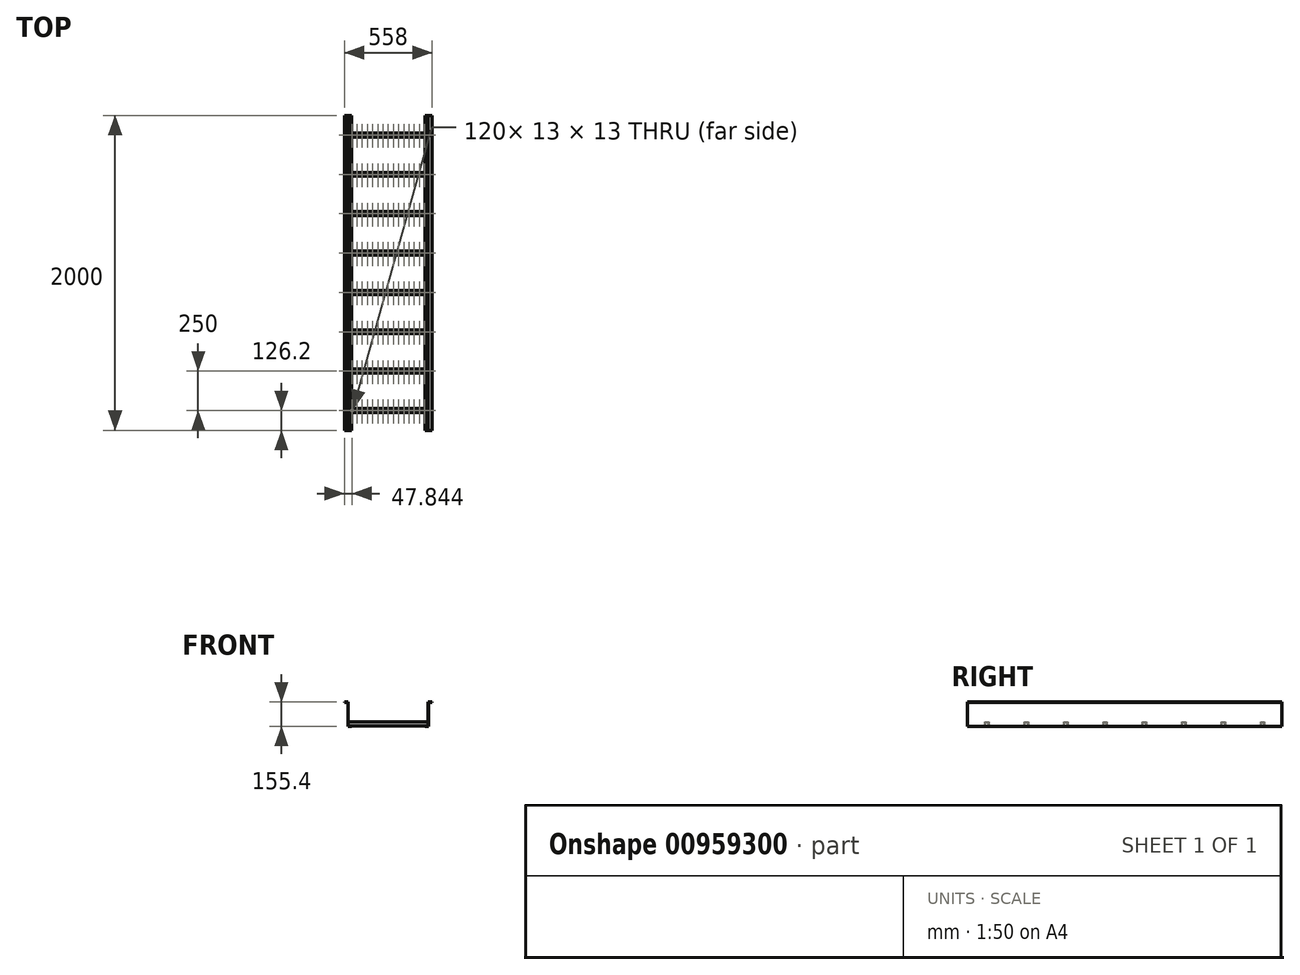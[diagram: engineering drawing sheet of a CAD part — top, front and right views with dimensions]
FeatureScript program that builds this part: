
annotation { "Feature Type Name" : "Feature", "Feature Type Description" : "" }
export const myFeature = defineFeature(function(context is Context, id is Id, definition is map)
    precondition{}
    {
        {
            var Q0;
            Q0=qCreatedBy(makeId("Front.planeOp"),FACE);
            var sketch = newSketch(context, id + "F0", { "sketchPlane" : qUnion([Q0])});
            skLineSegment(sketch, "E0", {"start": v(-136.9, 60.66) * mm, "end": v(-136.9, -91.74) * mm});
            skLineSegment(sketch, "E1", {"start": v(-136.9, -91.74) * mm, "end": v(-111.9, -91.74) * mm});
            skLineSegment(sketch, "E2", {"start": v(-111.9, -91.74) * mm, "end": v(-111.9, -88.74) * mm});
            skLineSegment(sketch, "E3", {"start": v(-111.9, -88.74) * mm, "end": v(-133.9, -88.74) * mm});
            skLineSegment(sketch, "E4", {"start": v(-133.9, -88.74) * mm, "end": v(-133.9, 63.66) * mm});
            skLineSegment(sketch, "E5", {"start": v(-133.9, 63.66) * mm, "end": v(-158.9, 63.66) * mm});
            skLineSegment(sketch, "E6", {"start": v(-158.9, 63.66) * mm, "end": v(-158.9, 60.66) * mm});
            skLineSegment(sketch, "E7", {"start": v(-158.9, 60.66) * mm, "end": v(-136.9, 60.66) * mm});
            skLineSegment(sketch, "E8", {"start": v(374.1, -88.74) * mm, "end": v(374.1, 63.66) * mm});
            skLineSegment(sketch, "E9", {"start": v(374.1, 63.66) * mm, "end": v(399.1, 63.66) * mm});
            skLineSegment(sketch, "E10", {"start": v(399.1, 63.66) * mm, "end": v(399.1, 60.66) * mm});
            skLineSegment(sketch, "E11", {"start": v(399.1, 60.66) * mm, "end": v(377.1, 60.66) * mm});
            skLineSegment(sketch, "E12", {"start": v(377.1, 60.66) * mm, "end": v(377.1, -91.74) * mm});
            skLineSegment(sketch, "E13", {"start": v(377.1, -91.74) * mm, "end": v(352.1, -91.74) * mm});
            skLineSegment(sketch, "E14", {"start": v(352.1, -91.74) * mm, "end": v(352.1, -88.74) * mm});
            skLineSegment(sketch, "E15", {"start": v(352.1, -88.74) * mm, "end": v(374.1, -88.74) * mm});
            skSolve(sketch);
        }
        {
            var Q0;
            Q0=makeQuery(id+"F0.imprint","IMPRINT",FACE,{"disambiguationData":[TD([[makeQuery(id+"F0.imprint","IMPRINT",EDGE,{"derivedFrom":sQuery(id+"F0.wireOp",EDGE,"E8")}),-1.0]])]});
            var Q1;
            Q1=makeQuery(id+"F0.imprint","IMPRINT",FACE,{"disambiguationData":[TD([[makeQuery(id+"F0.imprint","IMPRINT",EDGE,{"derivedFrom":sQuery(id+"F0.wireOp",EDGE,"E0")}),1.0]])]});
            extrude(context, id + "F1", {"entities" : qUnion([Q0, Q1]), "oppositeDirection" : true, "depth" : 2000 * mm, "offsetDistance" : 25 * mm});
        }
        {
            var Q0;
            Q0=makeQuery(id+"F1.opExtrude","SWEPT_FACE",FACE,{"disambiguationData":[OSD([sQuery(id+"F0.wireOp",EDGE,"E4")])]});
            var sketch = newSketch(context, id + "F2", { "sketchPlane" : qUnion([Q0])});
            skLineSegment(sketch, "E16", {"start": v(114, -88.74) * mm, "end": v(114, -64.34) * mm});
            skLineSegment(sketch, "E17", {"start": v(114, -64.34) * mm, "end": v(138.4, -64.34) * mm});
            skLineSegment(sketch, "E18", {"start": v(138.4, -64.34) * mm, "end": v(138.4, -88.74) * mm});
            skLineSegment(sketch, "E19", {"start": v(138.4, -88.74) * mm, "end": v(135.4, -88.74) * mm});
            skLineSegment(sketch, "E20", {"start": v(135.4, -88.74) * mm, "end": v(135.4, -67.34) * mm});
            skLineSegment(sketch, "E21", {"start": v(117, -88.74) * mm, "end": v(114, -88.74) * mm});
            skLineSegment(sketch, "E22", {"start": v(117, -88.74) * mm, "end": v(117, -67.34) * mm});
            skLineSegment(sketch, "E23", {"start": v(117, -67.34) * mm, "end": v(135.4, -67.34) * mm});
            skLineSegment(sketch, "E24.1.0.0", {"start": v(367, -67.34) * mm, "end": v(385.4, -67.34) * mm});
            skLineSegment(sketch, "E24.1.0.1", {"start": v(364, -64.34) * mm, "end": v(388.4, -64.34) * mm});
            skLineSegment(sketch, "E24.1.0.2", {"start": v(385.4, -88.74) * mm, "end": v(385.4, -67.34) * mm});
            skLineSegment(sketch, "E24.1.0.3", {"start": v(388.4, -64.34) * mm, "end": v(388.4, -88.74) * mm});
            skLineSegment(sketch, "E24.1.0.4", {"start": v(367, -88.74) * mm, "end": v(367, -67.34) * mm});
            skLineSegment(sketch, "E24.1.0.5", {"start": v(364, -88.74) * mm, "end": v(364, -64.34) * mm});
            skLineSegment(sketch, "E24.1.0.6", {"start": v(367, -88.74) * mm, "end": v(364, -88.74) * mm});
            skLineSegment(sketch, "E24.1.0.7", {"start": v(388.4, -88.74) * mm, "end": v(385.4, -88.74) * mm});
            skLineSegment(sketch, "E24.2.0.0", {"start": v(617, -67.34) * mm, "end": v(635.4, -67.34) * mm});
            skLineSegment(sketch, "E24.2.0.1", {"start": v(614, -64.34) * mm, "end": v(638.4, -64.34) * mm});
            skLineSegment(sketch, "E24.2.0.2", {"start": v(635.4, -88.74) * mm, "end": v(635.4, -67.34) * mm});
            skLineSegment(sketch, "E24.2.0.3", {"start": v(638.4, -64.34) * mm, "end": v(638.4, -88.74) * mm});
            skLineSegment(sketch, "E24.2.0.4", {"start": v(617, -88.74) * mm, "end": v(617, -67.34) * mm});
            skLineSegment(sketch, "E24.2.0.5", {"start": v(614, -88.74) * mm, "end": v(614, -64.34) * mm});
            skLineSegment(sketch, "E24.2.0.6", {"start": v(617, -88.74) * mm, "end": v(614, -88.74) * mm});
            skLineSegment(sketch, "E24.2.0.7", {"start": v(638.4, -88.74) * mm, "end": v(635.4, -88.74) * mm});
            skLineSegment(sketch, "E24.3.0.0", {"start": v(867, -67.34) * mm, "end": v(885.4, -67.34) * mm});
            skLineSegment(sketch, "E24.3.0.1", {"start": v(864, -64.34) * mm, "end": v(888.4, -64.34) * mm});
            skLineSegment(sketch, "E24.3.0.2", {"start": v(885.4, -88.74) * mm, "end": v(885.4, -67.34) * mm});
            skLineSegment(sketch, "E24.3.0.3", {"start": v(888.4, -64.34) * mm, "end": v(888.4, -88.74) * mm});
            skLineSegment(sketch, "E24.3.0.4", {"start": v(867, -88.74) * mm, "end": v(867, -67.34) * mm});
            skLineSegment(sketch, "E24.3.0.5", {"start": v(864, -88.74) * mm, "end": v(864, -64.34) * mm});
            skLineSegment(sketch, "E24.3.0.6", {"start": v(867, -88.74) * mm, "end": v(864, -88.74) * mm});
            skLineSegment(sketch, "E24.3.0.7", {"start": v(888.4, -88.74) * mm, "end": v(885.4, -88.74) * mm});
            skLineSegment(sketch, "E24.4.0.0", {"start": v(1117, -67.34) * mm, "end": v(1135.4, -67.34) * mm});
            skLineSegment(sketch, "E24.4.0.1", {"start": v(1114, -64.34) * mm, "end": v(1138.4, -64.34) * mm});
            skLineSegment(sketch, "E24.4.0.2", {"start": v(1135.4, -88.74) * mm, "end": v(1135.4, -67.34) * mm});
            skLineSegment(sketch, "E24.4.0.3", {"start": v(1138.4, -64.34) * mm, "end": v(1138.4, -88.74) * mm});
            skLineSegment(sketch, "E24.4.0.4", {"start": v(1117, -88.74) * mm, "end": v(1117, -67.34) * mm});
            skLineSegment(sketch, "E24.4.0.5", {"start": v(1114, -88.74) * mm, "end": v(1114, -64.34) * mm});
            skLineSegment(sketch, "E24.4.0.6", {"start": v(1117, -88.74) * mm, "end": v(1114, -88.74) * mm});
            skLineSegment(sketch, "E24.4.0.7", {"start": v(1138.4, -88.74) * mm, "end": v(1135.4, -88.74) * mm});
            skLineSegment(sketch, "E24.5.0.0", {"start": v(1367, -67.34) * mm, "end": v(1385.4, -67.34) * mm});
            skLineSegment(sketch, "E24.5.0.1", {"start": v(1364, -64.34) * mm, "end": v(1388.4, -64.34) * mm});
            skLineSegment(sketch, "E24.5.0.2", {"start": v(1385.4, -88.74) * mm, "end": v(1385.4, -67.34) * mm});
            skLineSegment(sketch, "E24.5.0.3", {"start": v(1388.4, -64.34) * mm, "end": v(1388.4, -88.74) * mm});
            skLineSegment(sketch, "E24.5.0.4", {"start": v(1367, -88.74) * mm, "end": v(1367, -67.34) * mm});
            skLineSegment(sketch, "E24.5.0.5", {"start": v(1364, -88.74) * mm, "end": v(1364, -64.34) * mm});
            skLineSegment(sketch, "E24.5.0.6", {"start": v(1367, -88.74) * mm, "end": v(1364, -88.74) * mm});
            skLineSegment(sketch, "E24.5.0.7", {"start": v(1388.4, -88.74) * mm, "end": v(1385.4, -88.74) * mm});
            skLineSegment(sketch, "E24.6.0.0", {"start": v(1617, -67.34) * mm, "end": v(1635.4, -67.34) * mm});
            skLineSegment(sketch, "E24.6.0.1", {"start": v(1614, -64.34) * mm, "end": v(1638.4, -64.34) * mm});
            skLineSegment(sketch, "E24.6.0.2", {"start": v(1635.4, -88.74) * mm, "end": v(1635.4, -67.34) * mm});
            skLineSegment(sketch, "E24.6.0.3", {"start": v(1638.4, -64.34) * mm, "end": v(1638.4, -88.74) * mm});
            skLineSegment(sketch, "E24.6.0.4", {"start": v(1617, -88.74) * mm, "end": v(1617, -67.34) * mm});
            skLineSegment(sketch, "E24.6.0.5", {"start": v(1614, -88.74) * mm, "end": v(1614, -64.34) * mm});
            skLineSegment(sketch, "E24.6.0.6", {"start": v(1617, -88.74) * mm, "end": v(1614, -88.74) * mm});
            skLineSegment(sketch, "E24.6.0.7", {"start": v(1638.4, -88.74) * mm, "end": v(1635.4, -88.74) * mm});
            skLineSegment(sketch, "E24.7.0.0", {"start": v(1867, -67.34) * mm, "end": v(1885.4, -67.34) * mm});
            skLineSegment(sketch, "E24.7.0.1", {"start": v(1864, -64.34) * mm, "end": v(1888.4, -64.34) * mm});
            skLineSegment(sketch, "E24.7.0.2", {"start": v(1885.4, -88.74) * mm, "end": v(1885.4, -67.34) * mm});
            skLineSegment(sketch, "E24.7.0.3", {"start": v(1888.4, -64.34) * mm, "end": v(1888.4, -88.74) * mm});
            skLineSegment(sketch, "E24.7.0.4", {"start": v(1867, -88.74) * mm, "end": v(1867, -67.34) * mm});
            skLineSegment(sketch, "E24.7.0.5", {"start": v(1864, -88.74) * mm, "end": v(1864, -64.34) * mm});
            skLineSegment(sketch, "E24.7.0.6", {"start": v(1867, -88.74) * mm, "end": v(1864, -88.74) * mm});
            skLineSegment(sketch, "E24.7.0.7", {"start": v(1888.4, -88.74) * mm, "end": v(1885.4, -88.74) * mm});
            skSolve(sketch);
        }
        {
            var Q0;
            Q0=makeQuery(id+"F2.imprint","IMPRINT",FACE,{"disambiguationData":[TD([[makeQuery(id+"F2.imprint","IMPRINT",EDGE,{"derivedFrom":sQuery(id+"F2.wireOp",EDGE,"E24.1.0.0")}),1.0]])]});
            var Q1;
            Q1=makeQuery(id+"F2.imprint","IMPRINT",FACE,{"disambiguationData":[TD([[makeQuery(id+"F2.imprint","IMPRINT",EDGE,{"derivedFrom":sQuery(id+"F2.wireOp",EDGE,"E24.2.0.0")}),1.0]])]});
            var Q2;
            Q2=makeQuery(id+"F2.imprint","IMPRINT",FACE,{"disambiguationData":[TD([[makeQuery(id+"F2.imprint","IMPRINT",EDGE,{"derivedFrom":sQuery(id+"F2.wireOp",EDGE,"E24.3.0.0")}),1.0]])]});
            var Q3;
            Q3=makeQuery(id+"F2.imprint","IMPRINT",FACE,{"disambiguationData":[TD([[makeQuery(id+"F2.imprint","IMPRINT",EDGE,{"derivedFrom":sQuery(id+"F2.wireOp",EDGE,"E24.4.0.0")}),1.0]])]});
            var Q4;
            Q4=makeQuery(id+"F2.imprint","IMPRINT",FACE,{"disambiguationData":[TD([[makeQuery(id+"F2.imprint","IMPRINT",EDGE,{"derivedFrom":sQuery(id+"F2.wireOp",EDGE,"E24.5.0.0")}),1.0]])]});
            var Q5;
            Q5=makeQuery(id+"F2.imprint","IMPRINT",FACE,{"disambiguationData":[TD([[makeQuery(id+"F2.imprint","IMPRINT",EDGE,{"derivedFrom":sQuery(id+"F2.wireOp",EDGE,"E24.6.0.0")}),1.0]])]});
            var Q6;
            Q6=makeQuery(id+"F2.imprint","IMPRINT",FACE,{"disambiguationData":[TD([[makeQuery(id+"F2.imprint","IMPRINT",EDGE,{"derivedFrom":sQuery(id+"F2.wireOp",EDGE,"E24.7.0.0")}),1.0]])]});
            var Q7;
            Q7=makeQuery(id+"F2.imprint","IMPRINT",FACE,{"disambiguationData":[TD([[makeQuery(id+"F2.imprint","IMPRINT",EDGE,{"derivedFrom":sQuery(id+"F2.wireOp",EDGE,"E16")}),-1.0]])]});
            extrude(context, id + "F3", {"entities" : qUnion([Q0, Q1, Q2, Q3, Q4, Q5, Q6, Q7]), "depth" : 508 * mm, "offsetDistance" : 25 * mm});
        }
        {
            var Q0;
            Q0=makeQuery(id+"F3.opExtrude","SWEPT_FACE",FACE,{"disambiguationData":[OSD([sQuery(id+"F2.wireOp",EDGE,"E17")])]});
            var sketch = newSketch(context, id + "F4", { "sketchPlane" : qUnion([Q0])});
            skLineSegment(sketch, "E25.bottom", {"start": v(-104.56, 119.7) * mm, "end": v(-117.56, 119.7) * mm});
            skLineSegment(sketch, "E25.top", {"start": v(-104.56, 132.7) * mm, "end": v(-117.56, 132.7) * mm});
            skLineSegment(sketch, "E25.left", {"start": v(-104.56, 119.7) * mm, "end": v(-104.56, 132.7) * mm});
            skLineSegment(sketch, "E25.right", {"start": v(-117.56, 119.7) * mm, "end": v(-117.56, 132.7) * mm});
            skPoint(sketch, "E25.middle", {"position": v(-111.06, 126.2) * mm});
            skLineSegment(sketch, "E26.0.1.0", {"start": v(-104.56, 382.7) * mm, "end": v(-117.56, 382.7) * mm});
            skLineSegment(sketch, "E26.0.1.1", {"start": v(-104.56, 369.7) * mm, "end": v(-104.56, 382.7) * mm});
            skLineSegment(sketch, "E26.0.1.2", {"start": v(-104.56, 369.7) * mm, "end": v(-117.56, 369.7) * mm});
            skPoint(sketch, "E26.0.1.3", {"position": v(-111.06, 376.2) * mm});
            skLineSegment(sketch, "E26.0.1.4", {"start": v(-117.56, 369.7) * mm, "end": v(-117.56, 382.7) * mm});
            skLineSegment(sketch, "E26.0.2.0", {"start": v(-104.56, 632.7) * mm, "end": v(-117.56, 632.7) * mm});
            skLineSegment(sketch, "E26.0.2.1", {"start": v(-104.56, 619.7) * mm, "end": v(-104.56, 632.7) * mm});
            skLineSegment(sketch, "E26.0.2.2", {"start": v(-104.56, 619.7) * mm, "end": v(-117.56, 619.7) * mm});
            skPoint(sketch, "E26.0.2.3", {"position": v(-111.06, 626.2) * mm});
            skLineSegment(sketch, "E26.0.2.4", {"start": v(-117.56, 619.7) * mm, "end": v(-117.56, 632.7) * mm});
            skLineSegment(sketch, "E26.0.3.0", {"start": v(-104.56, 882.7) * mm, "end": v(-117.56, 882.7) * mm});
            skLineSegment(sketch, "E26.0.3.1", {"start": v(-104.56, 869.7) * mm, "end": v(-104.56, 882.7) * mm});
            skLineSegment(sketch, "E26.0.3.2", {"start": v(-104.56, 869.7) * mm, "end": v(-117.56, 869.7) * mm});
            skPoint(sketch, "E26.0.3.3", {"position": v(-111.06, 876.2) * mm});
            skLineSegment(sketch, "E26.0.3.4", {"start": v(-117.56, 869.7) * mm, "end": v(-117.56, 882.7) * mm});
            skLineSegment(sketch, "E26.0.4.0", {"start": v(-104.56, 1132.7) * mm, "end": v(-117.56, 1132.7) * mm});
            skLineSegment(sketch, "E26.0.4.1", {"start": v(-104.56, 1119.7) * mm, "end": v(-104.56, 1132.7) * mm});
            skLineSegment(sketch, "E26.0.4.2", {"start": v(-104.56, 1119.7) * mm, "end": v(-117.56, 1119.7) * mm});
            skPoint(sketch, "E26.0.4.3", {"position": v(-111.06, 1126.2) * mm});
            skLineSegment(sketch, "E26.0.4.4", {"start": v(-117.56, 1119.7) * mm, "end": v(-117.56, 1132.7) * mm});
            skLineSegment(sketch, "E26.0.5.0", {"start": v(-104.56, 1382.7) * mm, "end": v(-117.56, 1382.7) * mm});
            skLineSegment(sketch, "E26.0.5.1", {"start": v(-104.56, 1369.7) * mm, "end": v(-104.56, 1382.7) * mm});
            skLineSegment(sketch, "E26.0.5.2", {"start": v(-104.56, 1369.7) * mm, "end": v(-117.56, 1369.7) * mm});
            skPoint(sketch, "E26.0.5.3", {"position": v(-111.06, 1376.2) * mm});
            skLineSegment(sketch, "E26.0.5.4", {"start": v(-117.56, 1369.7) * mm, "end": v(-117.56, 1382.7) * mm});
            skLineSegment(sketch, "E26.0.6.0", {"start": v(-104.56, 1632.7) * mm, "end": v(-117.56, 1632.7) * mm});
            skLineSegment(sketch, "E26.0.6.1", {"start": v(-104.56, 1619.7) * mm, "end": v(-104.56, 1632.7) * mm});
            skLineSegment(sketch, "E26.0.6.2", {"start": v(-104.56, 1619.7) * mm, "end": v(-117.56, 1619.7) * mm});
            skPoint(sketch, "E26.0.6.3", {"position": v(-111.06, 1626.2) * mm});
            skLineSegment(sketch, "E26.0.6.4", {"start": v(-117.56, 1619.7) * mm, "end": v(-117.56, 1632.7) * mm});
            skLineSegment(sketch, "E26.0.7.0", {"start": v(-104.56, 1882.7) * mm, "end": v(-117.56, 1882.7) * mm});
            skLineSegment(sketch, "E26.0.7.1", {"start": v(-104.56, 1869.7) * mm, "end": v(-104.56, 1882.7) * mm});
            skLineSegment(sketch, "E26.0.7.2", {"start": v(-104.56, 1869.7) * mm, "end": v(-117.56, 1869.7) * mm});
            skPoint(sketch, "E26.0.7.3", {"position": v(-111.06, 1876.2) * mm});
            skLineSegment(sketch, "E26.0.7.4", {"start": v(-117.56, 1869.7) * mm, "end": v(-117.56, 1882.7) * mm});
            skLineSegment(sketch, "E26.1.0.0", {"start": v(-71.56, 132.7) * mm, "end": v(-84.56, 132.7) * mm});
            skLineSegment(sketch, "E26.1.0.1", {"start": v(-71.56, 119.7) * mm, "end": v(-71.56, 132.7) * mm});
            skLineSegment(sketch, "E26.1.0.2", {"start": v(-71.56, 119.7) * mm, "end": v(-84.56, 119.7) * mm});
            skPoint(sketch, "E26.1.0.3", {"position": v(-78.06, 126.2) * mm});
            skLineSegment(sketch, "E26.1.0.4", {"start": v(-84.56, 119.7) * mm, "end": v(-84.56, 132.7) * mm});
            skLineSegment(sketch, "E26.1.1.0", {"start": v(-71.56, 382.7) * mm, "end": v(-84.56, 382.7) * mm});
            skLineSegment(sketch, "E26.1.1.1", {"start": v(-71.56, 369.7) * mm, "end": v(-71.56, 382.7) * mm});
            skLineSegment(sketch, "E26.1.1.2", {"start": v(-71.56, 369.7) * mm, "end": v(-84.56, 369.7) * mm});
            skPoint(sketch, "E26.1.1.3", {"position": v(-78.06, 376.2) * mm});
            skLineSegment(sketch, "E26.1.1.4", {"start": v(-84.56, 369.7) * mm, "end": v(-84.56, 382.7) * mm});
            skLineSegment(sketch, "E26.1.2.0", {"start": v(-71.56, 632.7) * mm, "end": v(-84.56, 632.7) * mm});
            skLineSegment(sketch, "E26.1.2.1", {"start": v(-71.56, 619.7) * mm, "end": v(-71.56, 632.7) * mm});
            skLineSegment(sketch, "E26.1.2.2", {"start": v(-71.56, 619.7) * mm, "end": v(-84.56, 619.7) * mm});
            skPoint(sketch, "E26.1.2.3", {"position": v(-78.06, 626.2) * mm});
            skLineSegment(sketch, "E26.1.2.4", {"start": v(-84.56, 619.7) * mm, "end": v(-84.56, 632.7) * mm});
            skLineSegment(sketch, "E26.1.3.0", {"start": v(-71.56, 882.7) * mm, "end": v(-84.56, 882.7) * mm});
            skLineSegment(sketch, "E26.1.3.1", {"start": v(-71.56, 869.7) * mm, "end": v(-71.56, 882.7) * mm});
            skLineSegment(sketch, "E26.1.3.2", {"start": v(-71.56, 869.7) * mm, "end": v(-84.56, 869.7) * mm});
            skPoint(sketch, "E26.1.3.3", {"position": v(-78.06, 876.2) * mm});
            skLineSegment(sketch, "E26.1.3.4", {"start": v(-84.56, 869.7) * mm, "end": v(-84.56, 882.7) * mm});
            skLineSegment(sketch, "E26.1.4.0", {"start": v(-71.56, 1132.7) * mm, "end": v(-84.56, 1132.7) * mm});
            skLineSegment(sketch, "E26.1.4.1", {"start": v(-71.56, 1119.7) * mm, "end": v(-71.56, 1132.7) * mm});
            skLineSegment(sketch, "E26.1.4.2", {"start": v(-71.56, 1119.7) * mm, "end": v(-84.56, 1119.7) * mm});
            skPoint(sketch, "E26.1.4.3", {"position": v(-78.06, 1126.2) * mm});
            skLineSegment(sketch, "E26.1.4.4", {"start": v(-84.56, 1119.7) * mm, "end": v(-84.56, 1132.7) * mm});
            skLineSegment(sketch, "E26.1.5.0", {"start": v(-71.56, 1382.7) * mm, "end": v(-84.56, 1382.7) * mm});
            skLineSegment(sketch, "E26.1.5.1", {"start": v(-71.56, 1369.7) * mm, "end": v(-71.56, 1382.7) * mm});
            skLineSegment(sketch, "E26.1.5.2", {"start": v(-71.56, 1369.7) * mm, "end": v(-84.56, 1369.7) * mm});
            skPoint(sketch, "E26.1.5.3", {"position": v(-78.06, 1376.2) * mm});
            skLineSegment(sketch, "E26.1.5.4", {"start": v(-84.56, 1369.7) * mm, "end": v(-84.56, 1382.7) * mm});
            skLineSegment(sketch, "E26.1.6.0", {"start": v(-71.56, 1632.7) * mm, "end": v(-84.56, 1632.7) * mm});
            skLineSegment(sketch, "E26.1.6.1", {"start": v(-71.56, 1619.7) * mm, "end": v(-71.56, 1632.7) * mm});
            skLineSegment(sketch, "E26.1.6.2", {"start": v(-71.56, 1619.7) * mm, "end": v(-84.56, 1619.7) * mm});
            skPoint(sketch, "E26.1.6.3", {"position": v(-78.06, 1626.2) * mm});
            skLineSegment(sketch, "E26.1.6.4", {"start": v(-84.56, 1619.7) * mm, "end": v(-84.56, 1632.7) * mm});
            skLineSegment(sketch, "E26.1.7.0", {"start": v(-71.56, 1882.7) * mm, "end": v(-84.56, 1882.7) * mm});
            skLineSegment(sketch, "E26.1.7.1", {"start": v(-71.56, 1869.7) * mm, "end": v(-71.56, 1882.7) * mm});
            skLineSegment(sketch, "E26.1.7.2", {"start": v(-71.56, 1869.7) * mm, "end": v(-84.56, 1869.7) * mm});
            skPoint(sketch, "E26.1.7.3", {"position": v(-78.06, 1876.2) * mm});
            skLineSegment(sketch, "E26.1.7.4", {"start": v(-84.56, 1869.7) * mm, "end": v(-84.56, 1882.7) * mm});
            skLineSegment(sketch, "E26.2.0.0", {"start": v(-38.56, 132.7) * mm, "end": v(-51.56, 132.7) * mm});
            skLineSegment(sketch, "E26.2.0.1", {"start": v(-38.56, 119.7) * mm, "end": v(-38.56, 132.7) * mm});
            skLineSegment(sketch, "E26.2.0.2", {"start": v(-38.56, 119.7) * mm, "end": v(-51.56, 119.7) * mm});
            skPoint(sketch, "E26.2.0.3", {"position": v(-45.06, 126.2) * mm});
            skLineSegment(sketch, "E26.2.0.4", {"start": v(-51.56, 119.7) * mm, "end": v(-51.56, 132.7) * mm});
            skLineSegment(sketch, "E26.2.1.0", {"start": v(-38.56, 382.7) * mm, "end": v(-51.56, 382.7) * mm});
            skLineSegment(sketch, "E26.2.1.1", {"start": v(-38.56, 369.7) * mm, "end": v(-38.56, 382.7) * mm});
            skLineSegment(sketch, "E26.2.1.2", {"start": v(-38.56, 369.7) * mm, "end": v(-51.56, 369.7) * mm});
            skPoint(sketch, "E26.2.1.3", {"position": v(-45.06, 376.2) * mm});
            skLineSegment(sketch, "E26.2.1.4", {"start": v(-51.56, 369.7) * mm, "end": v(-51.56, 382.7) * mm});
            skLineSegment(sketch, "E26.2.2.0", {"start": v(-38.56, 632.7) * mm, "end": v(-51.56, 632.7) * mm});
            skLineSegment(sketch, "E26.2.2.1", {"start": v(-38.56, 619.7) * mm, "end": v(-38.56, 632.7) * mm});
            skLineSegment(sketch, "E26.2.2.2", {"start": v(-38.56, 619.7) * mm, "end": v(-51.56, 619.7) * mm});
            skPoint(sketch, "E26.2.2.3", {"position": v(-45.06, 626.2) * mm});
            skLineSegment(sketch, "E26.2.2.4", {"start": v(-51.56, 619.7) * mm, "end": v(-51.56, 632.7) * mm});
            skLineSegment(sketch, "E26.2.3.0", {"start": v(-38.56, 882.7) * mm, "end": v(-51.56, 882.7) * mm});
            skLineSegment(sketch, "E26.2.3.1", {"start": v(-38.56, 869.7) * mm, "end": v(-38.56, 882.7) * mm});
            skLineSegment(sketch, "E26.2.3.2", {"start": v(-38.56, 869.7) * mm, "end": v(-51.56, 869.7) * mm});
            skPoint(sketch, "E26.2.3.3", {"position": v(-45.06, 876.2) * mm});
            skLineSegment(sketch, "E26.2.3.4", {"start": v(-51.56, 869.7) * mm, "end": v(-51.56, 882.7) * mm});
            skLineSegment(sketch, "E26.2.4.0", {"start": v(-38.56, 1132.7) * mm, "end": v(-51.56, 1132.7) * mm});
            skLineSegment(sketch, "E26.2.4.1", {"start": v(-38.56, 1119.7) * mm, "end": v(-38.56, 1132.7) * mm});
            skLineSegment(sketch, "E26.2.4.2", {"start": v(-38.56, 1119.7) * mm, "end": v(-51.56, 1119.7) * mm});
            skPoint(sketch, "E26.2.4.3", {"position": v(-45.06, 1126.2) * mm});
            skLineSegment(sketch, "E26.2.4.4", {"start": v(-51.56, 1119.7) * mm, "end": v(-51.56, 1132.7) * mm});
            skLineSegment(sketch, "E26.2.5.0", {"start": v(-38.56, 1382.7) * mm, "end": v(-51.56, 1382.7) * mm});
            skLineSegment(sketch, "E26.2.5.1", {"start": v(-38.56, 1369.7) * mm, "end": v(-38.56, 1382.7) * mm});
            skLineSegment(sketch, "E26.2.5.2", {"start": v(-38.56, 1369.7) * mm, "end": v(-51.56, 1369.7) * mm});
            skPoint(sketch, "E26.2.5.3", {"position": v(-45.06, 1376.2) * mm});
            skLineSegment(sketch, "E26.2.5.4", {"start": v(-51.56, 1369.7) * mm, "end": v(-51.56, 1382.7) * mm});
            skLineSegment(sketch, "E26.2.6.0", {"start": v(-38.56, 1632.7) * mm, "end": v(-51.56, 1632.7) * mm});
            skLineSegment(sketch, "E26.2.6.1", {"start": v(-38.56, 1619.7) * mm, "end": v(-38.56, 1632.7) * mm});
            skLineSegment(sketch, "E26.2.6.2", {"start": v(-38.56, 1619.7) * mm, "end": v(-51.56, 1619.7) * mm});
            skPoint(sketch, "E26.2.6.3", {"position": v(-45.06, 1626.2) * mm});
            skLineSegment(sketch, "E26.2.6.4", {"start": v(-51.56, 1619.7) * mm, "end": v(-51.56, 1632.7) * mm});
            skLineSegment(sketch, "E26.2.7.0", {"start": v(-38.56, 1882.7) * mm, "end": v(-51.56, 1882.7) * mm});
            skLineSegment(sketch, "E26.2.7.1", {"start": v(-38.56, 1869.7) * mm, "end": v(-38.56, 1882.7) * mm});
            skLineSegment(sketch, "E26.2.7.2", {"start": v(-38.56, 1869.7) * mm, "end": v(-51.56, 1869.7) * mm});
            skPoint(sketch, "E26.2.7.3", {"position": v(-45.06, 1876.2) * mm});
            skLineSegment(sketch, "E26.2.7.4", {"start": v(-51.56, 1869.7) * mm, "end": v(-51.56, 1882.7) * mm});
            skLineSegment(sketch, "E26.3.0.0", {"start": v(-5.56, 132.7) * mm, "end": v(-18.56, 132.7) * mm});
            skLineSegment(sketch, "E26.3.0.1", {"start": v(-5.56, 119.7) * mm, "end": v(-5.56, 132.7) * mm});
            skLineSegment(sketch, "E26.3.0.2", {"start": v(-5.56, 119.7) * mm, "end": v(-18.56, 119.7) * mm});
            skPoint(sketch, "E26.3.0.3", {"position": v(-12.06, 126.2) * mm});
            skLineSegment(sketch, "E26.3.0.4", {"start": v(-18.56, 119.7) * mm, "end": v(-18.56, 132.7) * mm});
            skLineSegment(sketch, "E26.3.1.0", {"start": v(-5.56, 382.7) * mm, "end": v(-18.56, 382.7) * mm});
            skLineSegment(sketch, "E26.3.1.1", {"start": v(-5.56, 369.7) * mm, "end": v(-5.56, 382.7) * mm});
            skLineSegment(sketch, "E26.3.1.2", {"start": v(-5.56, 369.7) * mm, "end": v(-18.56, 369.7) * mm});
            skPoint(sketch, "E26.3.1.3", {"position": v(-12.06, 376.2) * mm});
            skLineSegment(sketch, "E26.3.1.4", {"start": v(-18.56, 369.7) * mm, "end": v(-18.56, 382.7) * mm});
            skLineSegment(sketch, "E26.3.2.0", {"start": v(-5.56, 632.7) * mm, "end": v(-18.56, 632.7) * mm});
            skLineSegment(sketch, "E26.3.2.1", {"start": v(-5.56, 619.7) * mm, "end": v(-5.56, 632.7) * mm});
            skLineSegment(sketch, "E26.3.2.2", {"start": v(-5.56, 619.7) * mm, "end": v(-18.56, 619.7) * mm});
            skPoint(sketch, "E26.3.2.3", {"position": v(-12.06, 626.2) * mm});
            skLineSegment(sketch, "E26.3.2.4", {"start": v(-18.56, 619.7) * mm, "end": v(-18.56, 632.7) * mm});
            skLineSegment(sketch, "E26.3.3.0", {"start": v(-5.56, 882.7) * mm, "end": v(-18.56, 882.7) * mm});
            skLineSegment(sketch, "E26.3.3.1", {"start": v(-5.56, 869.7) * mm, "end": v(-5.56, 882.7) * mm});
            skLineSegment(sketch, "E26.3.3.2", {"start": v(-5.56, 869.7) * mm, "end": v(-18.56, 869.7) * mm});
            skPoint(sketch, "E26.3.3.3", {"position": v(-12.06, 876.2) * mm});
            skLineSegment(sketch, "E26.3.3.4", {"start": v(-18.56, 869.7) * mm, "end": v(-18.56, 882.7) * mm});
            skLineSegment(sketch, "E26.3.4.0", {"start": v(-5.56, 1132.7) * mm, "end": v(-18.56, 1132.7) * mm});
            skLineSegment(sketch, "E26.3.4.1", {"start": v(-5.56, 1119.7) * mm, "end": v(-5.56, 1132.7) * mm});
            skLineSegment(sketch, "E26.3.4.2", {"start": v(-5.56, 1119.7) * mm, "end": v(-18.56, 1119.7) * mm});
            skPoint(sketch, "E26.3.4.3", {"position": v(-12.06, 1126.2) * mm});
            skLineSegment(sketch, "E26.3.4.4", {"start": v(-18.56, 1119.7) * mm, "end": v(-18.56, 1132.7) * mm});
            skLineSegment(sketch, "E26.3.5.0", {"start": v(-5.56, 1382.7) * mm, "end": v(-18.56, 1382.7) * mm});
            skLineSegment(sketch, "E26.3.5.1", {"start": v(-5.56, 1369.7) * mm, "end": v(-5.56, 1382.7) * mm});
            skLineSegment(sketch, "E26.3.5.2", {"start": v(-5.56, 1369.7) * mm, "end": v(-18.56, 1369.7) * mm});
            skPoint(sketch, "E26.3.5.3", {"position": v(-12.06, 1376.2) * mm});
            skLineSegment(sketch, "E26.3.5.4", {"start": v(-18.56, 1369.7) * mm, "end": v(-18.56, 1382.7) * mm});
            skLineSegment(sketch, "E26.3.6.0", {"start": v(-5.56, 1632.7) * mm, "end": v(-18.56, 1632.7) * mm});
            skLineSegment(sketch, "E26.3.6.1", {"start": v(-5.56, 1619.7) * mm, "end": v(-5.56, 1632.7) * mm});
            skLineSegment(sketch, "E26.3.6.2", {"start": v(-5.56, 1619.7) * mm, "end": v(-18.56, 1619.7) * mm});
            skPoint(sketch, "E26.3.6.3", {"position": v(-12.06, 1626.2) * mm});
            skLineSegment(sketch, "E26.3.6.4", {"start": v(-18.56, 1619.7) * mm, "end": v(-18.56, 1632.7) * mm});
            skLineSegment(sketch, "E26.3.7.0", {"start": v(-5.56, 1882.7) * mm, "end": v(-18.56, 1882.7) * mm});
            skLineSegment(sketch, "E26.3.7.1", {"start": v(-5.56, 1869.7) * mm, "end": v(-5.56, 1882.7) * mm});
            skLineSegment(sketch, "E26.3.7.2", {"start": v(-5.56, 1869.7) * mm, "end": v(-18.56, 1869.7) * mm});
            skPoint(sketch, "E26.3.7.3", {"position": v(-12.06, 1876.2) * mm});
            skLineSegment(sketch, "E26.3.7.4", {"start": v(-18.56, 1869.7) * mm, "end": v(-18.56, 1882.7) * mm});
            skLineSegment(sketch, "E26.4.0.0", {"start": v(27.44, 132.7) * mm, "end": v(14.44, 132.7) * mm});
            skLineSegment(sketch, "E26.4.0.1", {"start": v(27.44, 119.7) * mm, "end": v(27.44, 132.7) * mm});
            skLineSegment(sketch, "E26.4.0.2", {"start": v(27.44, 119.7) * mm, "end": v(14.44, 119.7) * mm});
            skPoint(sketch, "E26.4.0.3", {"position": v(20.94, 126.2) * mm});
            skLineSegment(sketch, "E26.4.0.4", {"start": v(14.44, 119.7) * mm, "end": v(14.44, 132.7) * mm});
            skLineSegment(sketch, "E26.4.1.0", {"start": v(27.44, 382.7) * mm, "end": v(14.44, 382.7) * mm});
            skLineSegment(sketch, "E26.4.1.1", {"start": v(27.44, 369.7) * mm, "end": v(27.44, 382.7) * mm});
            skLineSegment(sketch, "E26.4.1.2", {"start": v(27.44, 369.7) * mm, "end": v(14.44, 369.7) * mm});
            skPoint(sketch, "E26.4.1.3", {"position": v(20.94, 376.2) * mm});
            skLineSegment(sketch, "E26.4.1.4", {"start": v(14.44, 369.7) * mm, "end": v(14.44, 382.7) * mm});
            skLineSegment(sketch, "E26.4.2.0", {"start": v(27.44, 632.7) * mm, "end": v(14.44, 632.7) * mm});
            skLineSegment(sketch, "E26.4.2.1", {"start": v(27.44, 619.7) * mm, "end": v(27.44, 632.7) * mm});
            skLineSegment(sketch, "E26.4.2.2", {"start": v(27.44, 619.7) * mm, "end": v(14.44, 619.7) * mm});
            skPoint(sketch, "E26.4.2.3", {"position": v(20.94, 626.2) * mm});
            skLineSegment(sketch, "E26.4.2.4", {"start": v(14.44, 619.7) * mm, "end": v(14.44, 632.7) * mm});
            skLineSegment(sketch, "E26.4.3.0", {"start": v(27.44, 882.7) * mm, "end": v(14.44, 882.7) * mm});
            skLineSegment(sketch, "E26.4.3.1", {"start": v(27.44, 869.7) * mm, "end": v(27.44, 882.7) * mm});
            skLineSegment(sketch, "E26.4.3.2", {"start": v(27.44, 869.7) * mm, "end": v(14.44, 869.7) * mm});
            skPoint(sketch, "E26.4.3.3", {"position": v(20.94, 876.2) * mm});
            skLineSegment(sketch, "E26.4.3.4", {"start": v(14.44, 869.7) * mm, "end": v(14.44, 882.7) * mm});
            skLineSegment(sketch, "E26.4.4.0", {"start": v(27.44, 1132.7) * mm, "end": v(14.44, 1132.7) * mm});
            skLineSegment(sketch, "E26.4.4.1", {"start": v(27.44, 1119.7) * mm, "end": v(27.44, 1132.7) * mm});
            skLineSegment(sketch, "E26.4.4.2", {"start": v(27.44, 1119.7) * mm, "end": v(14.44, 1119.7) * mm});
            skPoint(sketch, "E26.4.4.3", {"position": v(20.94, 1126.2) * mm});
            skLineSegment(sketch, "E26.4.4.4", {"start": v(14.44, 1119.7) * mm, "end": v(14.44, 1132.7) * mm});
            skLineSegment(sketch, "E26.4.5.0", {"start": v(27.44, 1382.7) * mm, "end": v(14.44, 1382.7) * mm});
            skLineSegment(sketch, "E26.4.5.1", {"start": v(27.44, 1369.7) * mm, "end": v(27.44, 1382.7) * mm});
            skLineSegment(sketch, "E26.4.5.2", {"start": v(27.44, 1369.7) * mm, "end": v(14.44, 1369.7) * mm});
            skPoint(sketch, "E26.4.5.3", {"position": v(20.94, 1376.2) * mm});
            skLineSegment(sketch, "E26.4.5.4", {"start": v(14.44, 1369.7) * mm, "end": v(14.44, 1382.7) * mm});
            skLineSegment(sketch, "E26.4.6.0", {"start": v(27.44, 1632.7) * mm, "end": v(14.44, 1632.7) * mm});
            skLineSegment(sketch, "E26.4.6.1", {"start": v(27.44, 1619.7) * mm, "end": v(27.44, 1632.7) * mm});
            skLineSegment(sketch, "E26.4.6.2", {"start": v(27.44, 1619.7) * mm, "end": v(14.44, 1619.7) * mm});
            skPoint(sketch, "E26.4.6.3", {"position": v(20.94, 1626.2) * mm});
            skLineSegment(sketch, "E26.4.6.4", {"start": v(14.44, 1619.7) * mm, "end": v(14.44, 1632.7) * mm});
            skLineSegment(sketch, "E26.4.7.0", {"start": v(27.44, 1882.7) * mm, "end": v(14.44, 1882.7) * mm});
            skLineSegment(sketch, "E26.4.7.1", {"start": v(27.44, 1869.7) * mm, "end": v(27.44, 1882.7) * mm});
            skLineSegment(sketch, "E26.4.7.2", {"start": v(27.44, 1869.7) * mm, "end": v(14.44, 1869.7) * mm});
            skPoint(sketch, "E26.4.7.3", {"position": v(20.94, 1876.2) * mm});
            skLineSegment(sketch, "E26.4.7.4", {"start": v(14.44, 1869.7) * mm, "end": v(14.44, 1882.7) * mm});
            skLineSegment(sketch, "E26.5.0.0", {"start": v(60.44, 132.7) * mm, "end": v(47.44, 132.7) * mm});
            skLineSegment(sketch, "E26.5.0.1", {"start": v(60.44, 119.7) * mm, "end": v(60.44, 132.7) * mm});
            skLineSegment(sketch, "E26.5.0.2", {"start": v(60.44, 119.7) * mm, "end": v(47.44, 119.7) * mm});
            skPoint(sketch, "E26.5.0.3", {"position": v(53.94, 126.2) * mm});
            skLineSegment(sketch, "E26.5.0.4", {"start": v(47.44, 119.7) * mm, "end": v(47.44, 132.7) * mm});
            skLineSegment(sketch, "E26.5.1.0", {"start": v(60.44, 382.7) * mm, "end": v(47.44, 382.7) * mm});
            skLineSegment(sketch, "E26.5.1.1", {"start": v(60.44, 369.7) * mm, "end": v(60.44, 382.7) * mm});
            skLineSegment(sketch, "E26.5.1.2", {"start": v(60.44, 369.7) * mm, "end": v(47.44, 369.7) * mm});
            skPoint(sketch, "E26.5.1.3", {"position": v(53.94, 376.2) * mm});
            skLineSegment(sketch, "E26.5.1.4", {"start": v(47.44, 369.7) * mm, "end": v(47.44, 382.7) * mm});
            skLineSegment(sketch, "E26.5.2.0", {"start": v(60.44, 632.7) * mm, "end": v(47.44, 632.7) * mm});
            skLineSegment(sketch, "E26.5.2.1", {"start": v(60.44, 619.7) * mm, "end": v(60.44, 632.7) * mm});
            skLineSegment(sketch, "E26.5.2.2", {"start": v(60.44, 619.7) * mm, "end": v(47.44, 619.7) * mm});
            skPoint(sketch, "E26.5.2.3", {"position": v(53.94, 626.2) * mm});
            skLineSegment(sketch, "E26.5.2.4", {"start": v(47.44, 619.7) * mm, "end": v(47.44, 632.7) * mm});
            skLineSegment(sketch, "E26.5.3.0", {"start": v(60.44, 882.7) * mm, "end": v(47.44, 882.7) * mm});
            skLineSegment(sketch, "E26.5.3.1", {"start": v(60.44, 869.7) * mm, "end": v(60.44, 882.7) * mm});
            skLineSegment(sketch, "E26.5.3.2", {"start": v(60.44, 869.7) * mm, "end": v(47.44, 869.7) * mm});
            skPoint(sketch, "E26.5.3.3", {"position": v(53.94, 876.2) * mm});
            skLineSegment(sketch, "E26.5.3.4", {"start": v(47.44, 869.7) * mm, "end": v(47.44, 882.7) * mm});
            skLineSegment(sketch, "E26.5.4.0", {"start": v(60.44, 1132.7) * mm, "end": v(47.44, 1132.7) * mm});
            skLineSegment(sketch, "E26.5.4.1", {"start": v(60.44, 1119.7) * mm, "end": v(60.44, 1132.7) * mm});
            skLineSegment(sketch, "E26.5.4.2", {"start": v(60.44, 1119.7) * mm, "end": v(47.44, 1119.7) * mm});
            skPoint(sketch, "E26.5.4.3", {"position": v(53.94, 1126.2) * mm});
            skLineSegment(sketch, "E26.5.4.4", {"start": v(47.44, 1119.7) * mm, "end": v(47.44, 1132.7) * mm});
            skLineSegment(sketch, "E26.5.5.0", {"start": v(60.44, 1382.7) * mm, "end": v(47.44, 1382.7) * mm});
            skLineSegment(sketch, "E26.5.5.1", {"start": v(60.44, 1369.7) * mm, "end": v(60.44, 1382.7) * mm});
            skLineSegment(sketch, "E26.5.5.2", {"start": v(60.44, 1369.7) * mm, "end": v(47.44, 1369.7) * mm});
            skPoint(sketch, "E26.5.5.3", {"position": v(53.94, 1376.2) * mm});
            skLineSegment(sketch, "E26.5.5.4", {"start": v(47.44, 1369.7) * mm, "end": v(47.44, 1382.7) * mm});
            skLineSegment(sketch, "E26.5.6.0", {"start": v(60.44, 1632.7) * mm, "end": v(47.44, 1632.7) * mm});
            skLineSegment(sketch, "E26.5.6.1", {"start": v(60.44, 1619.7) * mm, "end": v(60.44, 1632.7) * mm});
            skLineSegment(sketch, "E26.5.6.2", {"start": v(60.44, 1619.7) * mm, "end": v(47.44, 1619.7) * mm});
            skPoint(sketch, "E26.5.6.3", {"position": v(53.94, 1626.2) * mm});
            skLineSegment(sketch, "E26.5.6.4", {"start": v(47.44, 1619.7) * mm, "end": v(47.44, 1632.7) * mm});
            skLineSegment(sketch, "E26.5.7.0", {"start": v(60.44, 1882.7) * mm, "end": v(47.44, 1882.7) * mm});
            skLineSegment(sketch, "E26.5.7.1", {"start": v(60.44, 1869.7) * mm, "end": v(60.44, 1882.7) * mm});
            skLineSegment(sketch, "E26.5.7.2", {"start": v(60.44, 1869.7) * mm, "end": v(47.44, 1869.7) * mm});
            skPoint(sketch, "E26.5.7.3", {"position": v(53.94, 1876.2) * mm});
            skLineSegment(sketch, "E26.5.7.4", {"start": v(47.44, 1869.7) * mm, "end": v(47.44, 1882.7) * mm});
            skLineSegment(sketch, "E26.6.0.0", {"start": v(93.44, 132.7) * mm, "end": v(80.44, 132.7) * mm});
            skLineSegment(sketch, "E26.6.0.1", {"start": v(93.44, 119.7) * mm, "end": v(93.44, 132.7) * mm});
            skLineSegment(sketch, "E26.6.0.2", {"start": v(93.44, 119.7) * mm, "end": v(80.44, 119.7) * mm});
            skPoint(sketch, "E26.6.0.3", {"position": v(86.94, 126.2) * mm});
            skLineSegment(sketch, "E26.6.0.4", {"start": v(80.44, 119.7) * mm, "end": v(80.44, 132.7) * mm});
            skLineSegment(sketch, "E26.6.1.0", {"start": v(93.44, 382.7) * mm, "end": v(80.44, 382.7) * mm});
            skLineSegment(sketch, "E26.6.1.1", {"start": v(93.44, 369.7) * mm, "end": v(93.44, 382.7) * mm});
            skLineSegment(sketch, "E26.6.1.2", {"start": v(93.44, 369.7) * mm, "end": v(80.44, 369.7) * mm});
            skPoint(sketch, "E26.6.1.3", {"position": v(86.94, 376.2) * mm});
            skLineSegment(sketch, "E26.6.1.4", {"start": v(80.44, 369.7) * mm, "end": v(80.44, 382.7) * mm});
            skLineSegment(sketch, "E26.6.2.0", {"start": v(93.44, 632.7) * mm, "end": v(80.44, 632.7) * mm});
            skLineSegment(sketch, "E26.6.2.1", {"start": v(93.44, 619.7) * mm, "end": v(93.44, 632.7) * mm});
            skLineSegment(sketch, "E26.6.2.2", {"start": v(93.44, 619.7) * mm, "end": v(80.44, 619.7) * mm});
            skPoint(sketch, "E26.6.2.3", {"position": v(86.94, 626.2) * mm});
            skLineSegment(sketch, "E26.6.2.4", {"start": v(80.44, 619.7) * mm, "end": v(80.44, 632.7) * mm});
            skLineSegment(sketch, "E26.6.3.0", {"start": v(93.44, 882.7) * mm, "end": v(80.44, 882.7) * mm});
            skLineSegment(sketch, "E26.6.3.1", {"start": v(93.44, 869.7) * mm, "end": v(93.44, 882.7) * mm});
            skLineSegment(sketch, "E26.6.3.2", {"start": v(93.44, 869.7) * mm, "end": v(80.44, 869.7) * mm});
            skPoint(sketch, "E26.6.3.3", {"position": v(86.94, 876.2) * mm});
            skLineSegment(sketch, "E26.6.3.4", {"start": v(80.44, 869.7) * mm, "end": v(80.44, 882.7) * mm});
            skLineSegment(sketch, "E26.6.4.0", {"start": v(93.44, 1132.7) * mm, "end": v(80.44, 1132.7) * mm});
            skLineSegment(sketch, "E26.6.4.1", {"start": v(93.44, 1119.7) * mm, "end": v(93.44, 1132.7) * mm});
            skLineSegment(sketch, "E26.6.4.2", {"start": v(93.44, 1119.7) * mm, "end": v(80.44, 1119.7) * mm});
            skPoint(sketch, "E26.6.4.3", {"position": v(86.94, 1126.2) * mm});
            skLineSegment(sketch, "E26.6.4.4", {"start": v(80.44, 1119.7) * mm, "end": v(80.44, 1132.7) * mm});
            skLineSegment(sketch, "E26.6.5.0", {"start": v(93.44, 1382.7) * mm, "end": v(80.44, 1382.7) * mm});
            skLineSegment(sketch, "E26.6.5.1", {"start": v(93.44, 1369.7) * mm, "end": v(93.44, 1382.7) * mm});
            skLineSegment(sketch, "E26.6.5.2", {"start": v(93.44, 1369.7) * mm, "end": v(80.44, 1369.7) * mm});
            skPoint(sketch, "E26.6.5.3", {"position": v(86.94, 1376.2) * mm});
            skLineSegment(sketch, "E26.6.5.4", {"start": v(80.44, 1369.7) * mm, "end": v(80.44, 1382.7) * mm});
            skLineSegment(sketch, "E26.6.6.0", {"start": v(93.44, 1632.7) * mm, "end": v(80.44, 1632.7) * mm});
            skLineSegment(sketch, "E26.6.6.1", {"start": v(93.44, 1619.7) * mm, "end": v(93.44, 1632.7) * mm});
            skLineSegment(sketch, "E26.6.6.2", {"start": v(93.44, 1619.7) * mm, "end": v(80.44, 1619.7) * mm});
            skPoint(sketch, "E26.6.6.3", {"position": v(86.94, 1626.2) * mm});
            skLineSegment(sketch, "E26.6.6.4", {"start": v(80.44, 1619.7) * mm, "end": v(80.44, 1632.7) * mm});
            skLineSegment(sketch, "E26.6.7.0", {"start": v(93.44, 1882.7) * mm, "end": v(80.44, 1882.7) * mm});
            skLineSegment(sketch, "E26.6.7.1", {"start": v(93.44, 1869.7) * mm, "end": v(93.44, 1882.7) * mm});
            skLineSegment(sketch, "E26.6.7.2", {"start": v(93.44, 1869.7) * mm, "end": v(80.44, 1869.7) * mm});
            skPoint(sketch, "E26.6.7.3", {"position": v(86.94, 1876.2) * mm});
            skLineSegment(sketch, "E26.6.7.4", {"start": v(80.44, 1869.7) * mm, "end": v(80.44, 1882.7) * mm});
            skLineSegment(sketch, "E26.7.0.0", {"start": v(126.44, 132.7) * mm, "end": v(113.44, 132.7) * mm});
            skLineSegment(sketch, "E26.7.0.1", {"start": v(126.44, 119.7) * mm, "end": v(126.44, 132.7) * mm});
            skLineSegment(sketch, "E26.7.0.2", {"start": v(126.44, 119.7) * mm, "end": v(113.44, 119.7) * mm});
            skPoint(sketch, "E26.7.0.3", {"position": v(119.94, 126.2) * mm});
            skLineSegment(sketch, "E26.7.0.4", {"start": v(113.44, 119.7) * mm, "end": v(113.44, 132.7) * mm});
            skLineSegment(sketch, "E26.7.1.0", {"start": v(126.44, 382.7) * mm, "end": v(113.44, 382.7) * mm});
            skLineSegment(sketch, "E26.7.1.1", {"start": v(126.44, 369.7) * mm, "end": v(126.44, 382.7) * mm});
            skLineSegment(sketch, "E26.7.1.2", {"start": v(126.44, 369.7) * mm, "end": v(113.44, 369.7) * mm});
            skPoint(sketch, "E26.7.1.3", {"position": v(119.94, 376.2) * mm});
            skLineSegment(sketch, "E26.7.1.4", {"start": v(113.44, 369.7) * mm, "end": v(113.44, 382.7) * mm});
            skLineSegment(sketch, "E26.7.2.0", {"start": v(126.44, 632.7) * mm, "end": v(113.44, 632.7) * mm});
            skLineSegment(sketch, "E26.7.2.1", {"start": v(126.44, 619.7) * mm, "end": v(126.44, 632.7) * mm});
            skLineSegment(sketch, "E26.7.2.2", {"start": v(126.44, 619.7) * mm, "end": v(113.44, 619.7) * mm});
            skPoint(sketch, "E26.7.2.3", {"position": v(119.94, 626.2) * mm});
            skLineSegment(sketch, "E26.7.2.4", {"start": v(113.44, 619.7) * mm, "end": v(113.44, 632.7) * mm});
            skLineSegment(sketch, "E26.7.3.0", {"start": v(126.44, 882.7) * mm, "end": v(113.44, 882.7) * mm});
            skLineSegment(sketch, "E26.7.3.1", {"start": v(126.44, 869.7) * mm, "end": v(126.44, 882.7) * mm});
            skLineSegment(sketch, "E26.7.3.2", {"start": v(126.44, 869.7) * mm, "end": v(113.44, 869.7) * mm});
            skPoint(sketch, "E26.7.3.3", {"position": v(119.94, 876.2) * mm});
            skLineSegment(sketch, "E26.7.3.4", {"start": v(113.44, 869.7) * mm, "end": v(113.44, 882.7) * mm});
            skLineSegment(sketch, "E26.7.4.0", {"start": v(126.44, 1132.7) * mm, "end": v(113.44, 1132.7) * mm});
            skLineSegment(sketch, "E26.7.4.1", {"start": v(126.44, 1119.7) * mm, "end": v(126.44, 1132.7) * mm});
            skLineSegment(sketch, "E26.7.4.2", {"start": v(126.44, 1119.7) * mm, "end": v(113.44, 1119.7) * mm});
            skPoint(sketch, "E26.7.4.3", {"position": v(119.94, 1126.2) * mm});
            skLineSegment(sketch, "E26.7.4.4", {"start": v(113.44, 1119.7) * mm, "end": v(113.44, 1132.7) * mm});
            skLineSegment(sketch, "E26.7.5.0", {"start": v(126.44, 1382.7) * mm, "end": v(113.44, 1382.7) * mm});
            skLineSegment(sketch, "E26.7.5.1", {"start": v(126.44, 1369.7) * mm, "end": v(126.44, 1382.7) * mm});
            skLineSegment(sketch, "E26.7.5.2", {"start": v(126.44, 1369.7) * mm, "end": v(113.44, 1369.7) * mm});
            skPoint(sketch, "E26.7.5.3", {"position": v(119.94, 1376.2) * mm});
            skLineSegment(sketch, "E26.7.5.4", {"start": v(113.44, 1369.7) * mm, "end": v(113.44, 1382.7) * mm});
            skLineSegment(sketch, "E26.7.6.0", {"start": v(126.44, 1632.7) * mm, "end": v(113.44, 1632.7) * mm});
            skLineSegment(sketch, "E26.7.6.1", {"start": v(126.44, 1619.7) * mm, "end": v(126.44, 1632.7) * mm});
            skLineSegment(sketch, "E26.7.6.2", {"start": v(126.44, 1619.7) * mm, "end": v(113.44, 1619.7) * mm});
            skPoint(sketch, "E26.7.6.3", {"position": v(119.94, 1626.2) * mm});
            skLineSegment(sketch, "E26.7.6.4", {"start": v(113.44, 1619.7) * mm, "end": v(113.44, 1632.7) * mm});
            skLineSegment(sketch, "E26.7.7.0", {"start": v(126.44, 1882.7) * mm, "end": v(113.44, 1882.7) * mm});
            skLineSegment(sketch, "E26.7.7.1", {"start": v(126.44, 1869.7) * mm, "end": v(126.44, 1882.7) * mm});
            skLineSegment(sketch, "E26.7.7.2", {"start": v(126.44, 1869.7) * mm, "end": v(113.44, 1869.7) * mm});
            skPoint(sketch, "E26.7.7.3", {"position": v(119.94, 1876.2) * mm});
            skLineSegment(sketch, "E26.7.7.4", {"start": v(113.44, 1869.7) * mm, "end": v(113.44, 1882.7) * mm});
            skLineSegment(sketch, "E26.8.0.0", {"start": v(159.44, 132.7) * mm, "end": v(146.44, 132.7) * mm});
            skLineSegment(sketch, "E26.8.0.1", {"start": v(159.44, 119.7) * mm, "end": v(159.44, 132.7) * mm});
            skLineSegment(sketch, "E26.8.0.2", {"start": v(159.44, 119.7) * mm, "end": v(146.44, 119.7) * mm});
            skPoint(sketch, "E26.8.0.3", {"position": v(152.94, 126.2) * mm});
            skLineSegment(sketch, "E26.8.0.4", {"start": v(146.44, 119.7) * mm, "end": v(146.44, 132.7) * mm});
            skLineSegment(sketch, "E26.8.1.0", {"start": v(159.44, 382.7) * mm, "end": v(146.44, 382.7) * mm});
            skLineSegment(sketch, "E26.8.1.1", {"start": v(159.44, 369.7) * mm, "end": v(159.44, 382.7) * mm});
            skLineSegment(sketch, "E26.8.1.2", {"start": v(159.44, 369.7) * mm, "end": v(146.44, 369.7) * mm});
            skPoint(sketch, "E26.8.1.3", {"position": v(152.94, 376.2) * mm});
            skLineSegment(sketch, "E26.8.1.4", {"start": v(146.44, 369.7) * mm, "end": v(146.44, 382.7) * mm});
            skLineSegment(sketch, "E26.8.2.0", {"start": v(159.44, 632.7) * mm, "end": v(146.44, 632.7) * mm});
            skLineSegment(sketch, "E26.8.2.1", {"start": v(159.44, 619.7) * mm, "end": v(159.44, 632.7) * mm});
            skLineSegment(sketch, "E26.8.2.2", {"start": v(159.44, 619.7) * mm, "end": v(146.44, 619.7) * mm});
            skPoint(sketch, "E26.8.2.3", {"position": v(152.94, 626.2) * mm});
            skLineSegment(sketch, "E26.8.2.4", {"start": v(146.44, 619.7) * mm, "end": v(146.44, 632.7) * mm});
            skLineSegment(sketch, "E26.8.3.0", {"start": v(159.44, 882.7) * mm, "end": v(146.44, 882.7) * mm});
            skLineSegment(sketch, "E26.8.3.1", {"start": v(159.44, 869.7) * mm, "end": v(159.44, 882.7) * mm});
            skLineSegment(sketch, "E26.8.3.2", {"start": v(159.44, 869.7) * mm, "end": v(146.44, 869.7) * mm});
            skPoint(sketch, "E26.8.3.3", {"position": v(152.94, 876.2) * mm});
            skLineSegment(sketch, "E26.8.3.4", {"start": v(146.44, 869.7) * mm, "end": v(146.44, 882.7) * mm});
            skLineSegment(sketch, "E26.8.4.0", {"start": v(159.44, 1132.7) * mm, "end": v(146.44, 1132.7) * mm});
            skLineSegment(sketch, "E26.8.4.1", {"start": v(159.44, 1119.7) * mm, "end": v(159.44, 1132.7) * mm});
            skLineSegment(sketch, "E26.8.4.2", {"start": v(159.44, 1119.7) * mm, "end": v(146.44, 1119.7) * mm});
            skPoint(sketch, "E26.8.4.3", {"position": v(152.94, 1126.2) * mm});
            skLineSegment(sketch, "E26.8.4.4", {"start": v(146.44, 1119.7) * mm, "end": v(146.44, 1132.7) * mm});
            skLineSegment(sketch, "E26.8.5.0", {"start": v(159.44, 1382.7) * mm, "end": v(146.44, 1382.7) * mm});
            skLineSegment(sketch, "E26.8.5.1", {"start": v(159.44, 1369.7) * mm, "end": v(159.44, 1382.7) * mm});
            skLineSegment(sketch, "E26.8.5.2", {"start": v(159.44, 1369.7) * mm, "end": v(146.44, 1369.7) * mm});
            skPoint(sketch, "E26.8.5.3", {"position": v(152.94, 1376.2) * mm});
            skLineSegment(sketch, "E26.8.5.4", {"start": v(146.44, 1369.7) * mm, "end": v(146.44, 1382.7) * mm});
            skLineSegment(sketch, "E26.8.6.0", {"start": v(159.44, 1632.7) * mm, "end": v(146.44, 1632.7) * mm});
            skLineSegment(sketch, "E26.8.6.1", {"start": v(159.44, 1619.7) * mm, "end": v(159.44, 1632.7) * mm});
            skLineSegment(sketch, "E26.8.6.2", {"start": v(159.44, 1619.7) * mm, "end": v(146.44, 1619.7) * mm});
            skPoint(sketch, "E26.8.6.3", {"position": v(152.94, 1626.2) * mm});
            skLineSegment(sketch, "E26.8.6.4", {"start": v(146.44, 1619.7) * mm, "end": v(146.44, 1632.7) * mm});
            skLineSegment(sketch, "E26.8.7.0", {"start": v(159.44, 1882.7) * mm, "end": v(146.44, 1882.7) * mm});
            skLineSegment(sketch, "E26.8.7.1", {"start": v(159.44, 1869.7) * mm, "end": v(159.44, 1882.7) * mm});
            skLineSegment(sketch, "E26.8.7.2", {"start": v(159.44, 1869.7) * mm, "end": v(146.44, 1869.7) * mm});
            skPoint(sketch, "E26.8.7.3", {"position": v(152.94, 1876.2) * mm});
            skLineSegment(sketch, "E26.8.7.4", {"start": v(146.44, 1869.7) * mm, "end": v(146.44, 1882.7) * mm});
            skLineSegment(sketch, "E26.9.0.0", {"start": v(192.44, 132.7) * mm, "end": v(179.44, 132.7) * mm});
            skLineSegment(sketch, "E26.9.0.1", {"start": v(192.44, 119.7) * mm, "end": v(192.44, 132.7) * mm});
            skLineSegment(sketch, "E26.9.0.2", {"start": v(192.44, 119.7) * mm, "end": v(179.44, 119.7) * mm});
            skPoint(sketch, "E26.9.0.3", {"position": v(185.94, 126.2) * mm});
            skLineSegment(sketch, "E26.9.0.4", {"start": v(179.44, 119.7) * mm, "end": v(179.44, 132.7) * mm});
            skLineSegment(sketch, "E26.9.1.0", {"start": v(192.44, 382.7) * mm, "end": v(179.44, 382.7) * mm});
            skLineSegment(sketch, "E26.9.1.1", {"start": v(192.44, 369.7) * mm, "end": v(192.44, 382.7) * mm});
            skLineSegment(sketch, "E26.9.1.2", {"start": v(192.44, 369.7) * mm, "end": v(179.44, 369.7) * mm});
            skPoint(sketch, "E26.9.1.3", {"position": v(185.94, 376.2) * mm});
            skLineSegment(sketch, "E26.9.1.4", {"start": v(179.44, 369.7) * mm, "end": v(179.44, 382.7) * mm});
            skLineSegment(sketch, "E26.9.2.0", {"start": v(192.44, 632.7) * mm, "end": v(179.44, 632.7) * mm});
            skLineSegment(sketch, "E26.9.2.1", {"start": v(192.44, 619.7) * mm, "end": v(192.44, 632.7) * mm});
            skLineSegment(sketch, "E26.9.2.2", {"start": v(192.44, 619.7) * mm, "end": v(179.44, 619.7) * mm});
            skPoint(sketch, "E26.9.2.3", {"position": v(185.94, 626.2) * mm});
            skLineSegment(sketch, "E26.9.2.4", {"start": v(179.44, 619.7) * mm, "end": v(179.44, 632.7) * mm});
            skLineSegment(sketch, "E26.9.3.0", {"start": v(192.44, 882.7) * mm, "end": v(179.44, 882.7) * mm});
            skLineSegment(sketch, "E26.9.3.1", {"start": v(192.44, 869.7) * mm, "end": v(192.44, 882.7) * mm});
            skLineSegment(sketch, "E26.9.3.2", {"start": v(192.44, 869.7) * mm, "end": v(179.44, 869.7) * mm});
            skPoint(sketch, "E26.9.3.3", {"position": v(185.94, 876.2) * mm});
            skLineSegment(sketch, "E26.9.3.4", {"start": v(179.44, 869.7) * mm, "end": v(179.44, 882.7) * mm});
            skLineSegment(sketch, "E26.9.4.0", {"start": v(192.44, 1132.7) * mm, "end": v(179.44, 1132.7) * mm});
            skLineSegment(sketch, "E26.9.4.1", {"start": v(192.44, 1119.7) * mm, "end": v(192.44, 1132.7) * mm});
            skLineSegment(sketch, "E26.9.4.2", {"start": v(192.44, 1119.7) * mm, "end": v(179.44, 1119.7) * mm});
            skPoint(sketch, "E26.9.4.3", {"position": v(185.94, 1126.2) * mm});
            skLineSegment(sketch, "E26.9.4.4", {"start": v(179.44, 1119.7) * mm, "end": v(179.44, 1132.7) * mm});
            skLineSegment(sketch, "E26.9.5.0", {"start": v(192.44, 1382.7) * mm, "end": v(179.44, 1382.7) * mm});
            skLineSegment(sketch, "E26.9.5.1", {"start": v(192.44, 1369.7) * mm, "end": v(192.44, 1382.7) * mm});
            skLineSegment(sketch, "E26.9.5.2", {"start": v(192.44, 1369.7) * mm, "end": v(179.44, 1369.7) * mm});
            skPoint(sketch, "E26.9.5.3", {"position": v(185.94, 1376.2) * mm});
            skLineSegment(sketch, "E26.9.5.4", {"start": v(179.44, 1369.7) * mm, "end": v(179.44, 1382.7) * mm});
            skLineSegment(sketch, "E26.9.6.0", {"start": v(192.44, 1632.7) * mm, "end": v(179.44, 1632.7) * mm});
            skLineSegment(sketch, "E26.9.6.1", {"start": v(192.44, 1619.7) * mm, "end": v(192.44, 1632.7) * mm});
            skLineSegment(sketch, "E26.9.6.2", {"start": v(192.44, 1619.7) * mm, "end": v(179.44, 1619.7) * mm});
            skPoint(sketch, "E26.9.6.3", {"position": v(185.94, 1626.2) * mm});
            skLineSegment(sketch, "E26.9.6.4", {"start": v(179.44, 1619.7) * mm, "end": v(179.44, 1632.7) * mm});
            skLineSegment(sketch, "E26.9.7.0", {"start": v(192.44, 1882.7) * mm, "end": v(179.44, 1882.7) * mm});
            skLineSegment(sketch, "E26.9.7.1", {"start": v(192.44, 1869.7) * mm, "end": v(192.44, 1882.7) * mm});
            skLineSegment(sketch, "E26.9.7.2", {"start": v(192.44, 1869.7) * mm, "end": v(179.44, 1869.7) * mm});
            skPoint(sketch, "E26.9.7.3", {"position": v(185.94, 1876.2) * mm});
            skLineSegment(sketch, "E26.9.7.4", {"start": v(179.44, 1869.7) * mm, "end": v(179.44, 1882.7) * mm});
            skLineSegment(sketch, "E26.10.0.0", {"start": v(225.44, 132.7) * mm, "end": v(212.44, 132.7) * mm});
            skLineSegment(sketch, "E26.10.0.1", {"start": v(225.44, 119.7) * mm, "end": v(225.44, 132.7) * mm});
            skLineSegment(sketch, "E26.10.0.2", {"start": v(225.44, 119.7) * mm, "end": v(212.44, 119.7) * mm});
            skPoint(sketch, "E26.10.0.3", {"position": v(218.94, 126.2) * mm});
            skLineSegment(sketch, "E26.10.0.4", {"start": v(212.44, 119.7) * mm, "end": v(212.44, 132.7) * mm});
            skLineSegment(sketch, "E26.10.1.0", {"start": v(225.44, 382.7) * mm, "end": v(212.44, 382.7) * mm});
            skLineSegment(sketch, "E26.10.1.1", {"start": v(225.44, 369.7) * mm, "end": v(225.44, 382.7) * mm});
            skLineSegment(sketch, "E26.10.1.2", {"start": v(225.44, 369.7) * mm, "end": v(212.44, 369.7) * mm});
            skPoint(sketch, "E26.10.1.3", {"position": v(218.94, 376.2) * mm});
            skLineSegment(sketch, "E26.10.1.4", {"start": v(212.44, 369.7) * mm, "end": v(212.44, 382.7) * mm});
            skLineSegment(sketch, "E26.10.2.0", {"start": v(225.44, 632.7) * mm, "end": v(212.44, 632.7) * mm});
            skLineSegment(sketch, "E26.10.2.1", {"start": v(225.44, 619.7) * mm, "end": v(225.44, 632.7) * mm});
            skLineSegment(sketch, "E26.10.2.2", {"start": v(225.44, 619.7) * mm, "end": v(212.44, 619.7) * mm});
            skPoint(sketch, "E26.10.2.3", {"position": v(218.94, 626.2) * mm});
            skLineSegment(sketch, "E26.10.2.4", {"start": v(212.44, 619.7) * mm, "end": v(212.44, 632.7) * mm});
            skLineSegment(sketch, "E26.10.3.0", {"start": v(225.44, 882.7) * mm, "end": v(212.44, 882.7) * mm});
            skLineSegment(sketch, "E26.10.3.1", {"start": v(225.44, 869.7) * mm, "end": v(225.44, 882.7) * mm});
            skLineSegment(sketch, "E26.10.3.2", {"start": v(225.44, 869.7) * mm, "end": v(212.44, 869.7) * mm});
            skPoint(sketch, "E26.10.3.3", {"position": v(218.94, 876.2) * mm});
            skLineSegment(sketch, "E26.10.3.4", {"start": v(212.44, 869.7) * mm, "end": v(212.44, 882.7) * mm});
            skLineSegment(sketch, "E26.10.4.0", {"start": v(225.44, 1132.7) * mm, "end": v(212.44, 1132.7) * mm});
            skLineSegment(sketch, "E26.10.4.1", {"start": v(225.44, 1119.7) * mm, "end": v(225.44, 1132.7) * mm});
            skLineSegment(sketch, "E26.10.4.2", {"start": v(225.44, 1119.7) * mm, "end": v(212.44, 1119.7) * mm});
            skPoint(sketch, "E26.10.4.3", {"position": v(218.94, 1126.2) * mm});
            skLineSegment(sketch, "E26.10.4.4", {"start": v(212.44, 1119.7) * mm, "end": v(212.44, 1132.7) * mm});
            skLineSegment(sketch, "E26.10.5.0", {"start": v(225.44, 1382.7) * mm, "end": v(212.44, 1382.7) * mm});
            skLineSegment(sketch, "E26.10.5.1", {"start": v(225.44, 1369.7) * mm, "end": v(225.44, 1382.7) * mm});
            skLineSegment(sketch, "E26.10.5.2", {"start": v(225.44, 1369.7) * mm, "end": v(212.44, 1369.7) * mm});
            skPoint(sketch, "E26.10.5.3", {"position": v(218.94, 1376.2) * mm});
            skLineSegment(sketch, "E26.10.5.4", {"start": v(212.44, 1369.7) * mm, "end": v(212.44, 1382.7) * mm});
            skLineSegment(sketch, "E26.10.6.0", {"start": v(225.44, 1632.7) * mm, "end": v(212.44, 1632.7) * mm});
            skLineSegment(sketch, "E26.10.6.1", {"start": v(225.44, 1619.7) * mm, "end": v(225.44, 1632.7) * mm});
            skLineSegment(sketch, "E26.10.6.2", {"start": v(225.44, 1619.7) * mm, "end": v(212.44, 1619.7) * mm});
            skPoint(sketch, "E26.10.6.3", {"position": v(218.94, 1626.2) * mm});
            skLineSegment(sketch, "E26.10.6.4", {"start": v(212.44, 1619.7) * mm, "end": v(212.44, 1632.7) * mm});
            skLineSegment(sketch, "E26.10.7.0", {"start": v(225.44, 1882.7) * mm, "end": v(212.44, 1882.7) * mm});
            skLineSegment(sketch, "E26.10.7.1", {"start": v(225.44, 1869.7) * mm, "end": v(225.44, 1882.7) * mm});
            skLineSegment(sketch, "E26.10.7.2", {"start": v(225.44, 1869.7) * mm, "end": v(212.44, 1869.7) * mm});
            skPoint(sketch, "E26.10.7.3", {"position": v(218.94, 1876.2) * mm});
            skLineSegment(sketch, "E26.10.7.4", {"start": v(212.44, 1869.7) * mm, "end": v(212.44, 1882.7) * mm});
            skLineSegment(sketch, "E26.11.0.0", {"start": v(258.44, 132.7) * mm, "end": v(245.44, 132.7) * mm});
            skLineSegment(sketch, "E26.11.0.1", {"start": v(258.44, 119.7) * mm, "end": v(258.44, 132.7) * mm});
            skLineSegment(sketch, "E26.11.0.2", {"start": v(258.44, 119.7) * mm, "end": v(245.44, 119.7) * mm});
            skPoint(sketch, "E26.11.0.3", {"position": v(251.94, 126.2) * mm});
            skLineSegment(sketch, "E26.11.0.4", {"start": v(245.44, 119.7) * mm, "end": v(245.44, 132.7) * mm});
            skLineSegment(sketch, "E26.11.1.0", {"start": v(258.44, 382.7) * mm, "end": v(245.44, 382.7) * mm});
            skLineSegment(sketch, "E26.11.1.1", {"start": v(258.44, 369.7) * mm, "end": v(258.44, 382.7) * mm});
            skLineSegment(sketch, "E26.11.1.2", {"start": v(258.44, 369.7) * mm, "end": v(245.44, 369.7) * mm});
            skPoint(sketch, "E26.11.1.3", {"position": v(251.94, 376.2) * mm});
            skLineSegment(sketch, "E26.11.1.4", {"start": v(245.44, 369.7) * mm, "end": v(245.44, 382.7) * mm});
            skLineSegment(sketch, "E26.11.2.0", {"start": v(258.44, 632.7) * mm, "end": v(245.44, 632.7) * mm});
            skLineSegment(sketch, "E26.11.2.1", {"start": v(258.44, 619.7) * mm, "end": v(258.44, 632.7) * mm});
            skLineSegment(sketch, "E26.11.2.2", {"start": v(258.44, 619.7) * mm, "end": v(245.44, 619.7) * mm});
            skPoint(sketch, "E26.11.2.3", {"position": v(251.94, 626.2) * mm});
            skLineSegment(sketch, "E26.11.2.4", {"start": v(245.44, 619.7) * mm, "end": v(245.44, 632.7) * mm});
            skLineSegment(sketch, "E26.11.3.0", {"start": v(258.44, 882.7) * mm, "end": v(245.44, 882.7) * mm});
            skLineSegment(sketch, "E26.11.3.1", {"start": v(258.44, 869.7) * mm, "end": v(258.44, 882.7) * mm});
            skLineSegment(sketch, "E26.11.3.2", {"start": v(258.44, 869.7) * mm, "end": v(245.44, 869.7) * mm});
            skPoint(sketch, "E26.11.3.3", {"position": v(251.94, 876.2) * mm});
            skLineSegment(sketch, "E26.11.3.4", {"start": v(245.44, 869.7) * mm, "end": v(245.44, 882.7) * mm});
            skLineSegment(sketch, "E26.11.4.0", {"start": v(258.44, 1132.7) * mm, "end": v(245.44, 1132.7) * mm});
            skLineSegment(sketch, "E26.11.4.1", {"start": v(258.44, 1119.7) * mm, "end": v(258.44, 1132.7) * mm});
            skLineSegment(sketch, "E26.11.4.2", {"start": v(258.44, 1119.7) * mm, "end": v(245.44, 1119.7) * mm});
            skPoint(sketch, "E26.11.4.3", {"position": v(251.94, 1126.2) * mm});
            skLineSegment(sketch, "E26.11.4.4", {"start": v(245.44, 1119.7) * mm, "end": v(245.44, 1132.7) * mm});
            skLineSegment(sketch, "E26.11.5.0", {"start": v(258.44, 1382.7) * mm, "end": v(245.44, 1382.7) * mm});
            skLineSegment(sketch, "E26.11.5.1", {"start": v(258.44, 1369.7) * mm, "end": v(258.44, 1382.7) * mm});
            skLineSegment(sketch, "E26.11.5.2", {"start": v(258.44, 1369.7) * mm, "end": v(245.44, 1369.7) * mm});
            skPoint(sketch, "E26.11.5.3", {"position": v(251.94, 1376.2) * mm});
            skLineSegment(sketch, "E26.11.5.4", {"start": v(245.44, 1369.7) * mm, "end": v(245.44, 1382.7) * mm});
            skLineSegment(sketch, "E26.11.6.0", {"start": v(258.44, 1632.7) * mm, "end": v(245.44, 1632.7) * mm});
            skLineSegment(sketch, "E26.11.6.1", {"start": v(258.44, 1619.7) * mm, "end": v(258.44, 1632.7) * mm});
            skLineSegment(sketch, "E26.11.6.2", {"start": v(258.44, 1619.7) * mm, "end": v(245.44, 1619.7) * mm});
            skPoint(sketch, "E26.11.6.3", {"position": v(251.94, 1626.2) * mm});
            skLineSegment(sketch, "E26.11.6.4", {"start": v(245.44, 1619.7) * mm, "end": v(245.44, 1632.7) * mm});
            skLineSegment(sketch, "E26.11.7.0", {"start": v(258.44, 1882.7) * mm, "end": v(245.44, 1882.7) * mm});
            skLineSegment(sketch, "E26.11.7.1", {"start": v(258.44, 1869.7) * mm, "end": v(258.44, 1882.7) * mm});
            skLineSegment(sketch, "E26.11.7.2", {"start": v(258.44, 1869.7) * mm, "end": v(245.44, 1869.7) * mm});
            skPoint(sketch, "E26.11.7.3", {"position": v(251.94, 1876.2) * mm});
            skLineSegment(sketch, "E26.11.7.4", {"start": v(245.44, 1869.7) * mm, "end": v(245.44, 1882.7) * mm});
            skLineSegment(sketch, "E26.12.0.0", {"start": v(291.44, 132.7) * mm, "end": v(278.44, 132.7) * mm});
            skLineSegment(sketch, "E26.12.0.1", {"start": v(291.44, 119.7) * mm, "end": v(291.44, 132.7) * mm});
            skLineSegment(sketch, "E26.12.0.2", {"start": v(291.44, 119.7) * mm, "end": v(278.44, 119.7) * mm});
            skPoint(sketch, "E26.12.0.3", {"position": v(284.94, 126.2) * mm});
            skLineSegment(sketch, "E26.12.0.4", {"start": v(278.44, 119.7) * mm, "end": v(278.44, 132.7) * mm});
            skLineSegment(sketch, "E26.12.1.0", {"start": v(291.44, 382.7) * mm, "end": v(278.44, 382.7) * mm});
            skLineSegment(sketch, "E26.12.1.1", {"start": v(291.44, 369.7) * mm, "end": v(291.44, 382.7) * mm});
            skLineSegment(sketch, "E26.12.1.2", {"start": v(291.44, 369.7) * mm, "end": v(278.44, 369.7) * mm});
            skPoint(sketch, "E26.12.1.3", {"position": v(284.94, 376.2) * mm});
            skLineSegment(sketch, "E26.12.1.4", {"start": v(278.44, 369.7) * mm, "end": v(278.44, 382.7) * mm});
            skLineSegment(sketch, "E26.12.2.0", {"start": v(291.44, 632.7) * mm, "end": v(278.44, 632.7) * mm});
            skLineSegment(sketch, "E26.12.2.1", {"start": v(291.44, 619.7) * mm, "end": v(291.44, 632.7) * mm});
            skLineSegment(sketch, "E26.12.2.2", {"start": v(291.44, 619.7) * mm, "end": v(278.44, 619.7) * mm});
            skPoint(sketch, "E26.12.2.3", {"position": v(284.94, 626.2) * mm});
            skLineSegment(sketch, "E26.12.2.4", {"start": v(278.44, 619.7) * mm, "end": v(278.44, 632.7) * mm});
            skLineSegment(sketch, "E26.12.3.0", {"start": v(291.44, 882.7) * mm, "end": v(278.44, 882.7) * mm});
            skLineSegment(sketch, "E26.12.3.1", {"start": v(291.44, 869.7) * mm, "end": v(291.44, 882.7) * mm});
            skLineSegment(sketch, "E26.12.3.2", {"start": v(291.44, 869.7) * mm, "end": v(278.44, 869.7) * mm});
            skPoint(sketch, "E26.12.3.3", {"position": v(284.94, 876.2) * mm});
            skLineSegment(sketch, "E26.12.3.4", {"start": v(278.44, 869.7) * mm, "end": v(278.44, 882.7) * mm});
            skLineSegment(sketch, "E26.12.4.0", {"start": v(291.44, 1132.7) * mm, "end": v(278.44, 1132.7) * mm});
            skLineSegment(sketch, "E26.12.4.1", {"start": v(291.44, 1119.7) * mm, "end": v(291.44, 1132.7) * mm});
            skLineSegment(sketch, "E26.12.4.2", {"start": v(291.44, 1119.7) * mm, "end": v(278.44, 1119.7) * mm});
            skPoint(sketch, "E26.12.4.3", {"position": v(284.94, 1126.2) * mm});
            skLineSegment(sketch, "E26.12.4.4", {"start": v(278.44, 1119.7) * mm, "end": v(278.44, 1132.7) * mm});
            skLineSegment(sketch, "E26.12.5.0", {"start": v(291.44, 1382.7) * mm, "end": v(278.44, 1382.7) * mm});
            skLineSegment(sketch, "E26.12.5.1", {"start": v(291.44, 1369.7) * mm, "end": v(291.44, 1382.7) * mm});
            skLineSegment(sketch, "E26.12.5.2", {"start": v(291.44, 1369.7) * mm, "end": v(278.44, 1369.7) * mm});
            skPoint(sketch, "E26.12.5.3", {"position": v(284.94, 1376.2) * mm});
            skLineSegment(sketch, "E26.12.5.4", {"start": v(278.44, 1369.7) * mm, "end": v(278.44, 1382.7) * mm});
            skLineSegment(sketch, "E26.12.6.0", {"start": v(291.44, 1632.7) * mm, "end": v(278.44, 1632.7) * mm});
            skLineSegment(sketch, "E26.12.6.1", {"start": v(291.44, 1619.7) * mm, "end": v(291.44, 1632.7) * mm});
            skLineSegment(sketch, "E26.12.6.2", {"start": v(291.44, 1619.7) * mm, "end": v(278.44, 1619.7) * mm});
            skPoint(sketch, "E26.12.6.3", {"position": v(284.94, 1626.2) * mm});
            skLineSegment(sketch, "E26.12.6.4", {"start": v(278.44, 1619.7) * mm, "end": v(278.44, 1632.7) * mm});
            skLineSegment(sketch, "E26.12.7.0", {"start": v(291.44, 1882.7) * mm, "end": v(278.44, 1882.7) * mm});
            skLineSegment(sketch, "E26.12.7.1", {"start": v(291.44, 1869.7) * mm, "end": v(291.44, 1882.7) * mm});
            skLineSegment(sketch, "E26.12.7.2", {"start": v(291.44, 1869.7) * mm, "end": v(278.44, 1869.7) * mm});
            skPoint(sketch, "E26.12.7.3", {"position": v(284.94, 1876.2) * mm});
            skLineSegment(sketch, "E26.12.7.4", {"start": v(278.44, 1869.7) * mm, "end": v(278.44, 1882.7) * mm});
            skLineSegment(sketch, "E26.13.0.0", {"start": v(324.44, 132.7) * mm, "end": v(311.44, 132.7) * mm});
            skLineSegment(sketch, "E26.13.0.1", {"start": v(324.44, 119.7) * mm, "end": v(324.44, 132.7) * mm});
            skLineSegment(sketch, "E26.13.0.2", {"start": v(324.44, 119.7) * mm, "end": v(311.44, 119.7) * mm});
            skPoint(sketch, "E26.13.0.3", {"position": v(317.94, 126.2) * mm});
            skLineSegment(sketch, "E26.13.0.4", {"start": v(311.44, 119.7) * mm, "end": v(311.44, 132.7) * mm});
            skLineSegment(sketch, "E26.13.1.0", {"start": v(324.44, 382.7) * mm, "end": v(311.44, 382.7) * mm});
            skLineSegment(sketch, "E26.13.1.1", {"start": v(324.44, 369.7) * mm, "end": v(324.44, 382.7) * mm});
            skLineSegment(sketch, "E26.13.1.2", {"start": v(324.44, 369.7) * mm, "end": v(311.44, 369.7) * mm});
            skPoint(sketch, "E26.13.1.3", {"position": v(317.94, 376.2) * mm});
            skLineSegment(sketch, "E26.13.1.4", {"start": v(311.44, 369.7) * mm, "end": v(311.44, 382.7) * mm});
            skLineSegment(sketch, "E26.13.2.0", {"start": v(324.44, 632.7) * mm, "end": v(311.44, 632.7) * mm});
            skLineSegment(sketch, "E26.13.2.1", {"start": v(324.44, 619.7) * mm, "end": v(324.44, 632.7) * mm});
            skLineSegment(sketch, "E26.13.2.2", {"start": v(324.44, 619.7) * mm, "end": v(311.44, 619.7) * mm});
            skPoint(sketch, "E26.13.2.3", {"position": v(317.94, 626.2) * mm});
            skLineSegment(sketch, "E26.13.2.4", {"start": v(311.44, 619.7) * mm, "end": v(311.44, 632.7) * mm});
            skLineSegment(sketch, "E26.13.3.0", {"start": v(324.44, 882.7) * mm, "end": v(311.44, 882.7) * mm});
            skLineSegment(sketch, "E26.13.3.1", {"start": v(324.44, 869.7) * mm, "end": v(324.44, 882.7) * mm});
            skLineSegment(sketch, "E26.13.3.2", {"start": v(324.44, 869.7) * mm, "end": v(311.44, 869.7) * mm});
            skPoint(sketch, "E26.13.3.3", {"position": v(317.94, 876.2) * mm});
            skLineSegment(sketch, "E26.13.3.4", {"start": v(311.44, 869.7) * mm, "end": v(311.44, 882.7) * mm});
            skLineSegment(sketch, "E26.13.4.0", {"start": v(324.44, 1132.7) * mm, "end": v(311.44, 1132.7) * mm});
            skLineSegment(sketch, "E26.13.4.1", {"start": v(324.44, 1119.7) * mm, "end": v(324.44, 1132.7) * mm});
            skLineSegment(sketch, "E26.13.4.2", {"start": v(324.44, 1119.7) * mm, "end": v(311.44, 1119.7) * mm});
            skPoint(sketch, "E26.13.4.3", {"position": v(317.94, 1126.2) * mm});
            skLineSegment(sketch, "E26.13.4.4", {"start": v(311.44, 1119.7) * mm, "end": v(311.44, 1132.7) * mm});
            skLineSegment(sketch, "E26.13.5.0", {"start": v(324.44, 1382.7) * mm, "end": v(311.44, 1382.7) * mm});
            skLineSegment(sketch, "E26.13.5.1", {"start": v(324.44, 1369.7) * mm, "end": v(324.44, 1382.7) * mm});
            skLineSegment(sketch, "E26.13.5.2", {"start": v(324.44, 1369.7) * mm, "end": v(311.44, 1369.7) * mm});
            skPoint(sketch, "E26.13.5.3", {"position": v(317.94, 1376.2) * mm});
            skLineSegment(sketch, "E26.13.5.4", {"start": v(311.44, 1369.7) * mm, "end": v(311.44, 1382.7) * mm});
            skLineSegment(sketch, "E26.13.6.0", {"start": v(324.44, 1632.7) * mm, "end": v(311.44, 1632.7) * mm});
            skLineSegment(sketch, "E26.13.6.1", {"start": v(324.44, 1619.7) * mm, "end": v(324.44, 1632.7) * mm});
            skLineSegment(sketch, "E26.13.6.2", {"start": v(324.44, 1619.7) * mm, "end": v(311.44, 1619.7) * mm});
            skPoint(sketch, "E26.13.6.3", {"position": v(317.94, 1626.2) * mm});
            skLineSegment(sketch, "E26.13.6.4", {"start": v(311.44, 1619.7) * mm, "end": v(311.44, 1632.7) * mm});
            skLineSegment(sketch, "E26.13.7.0", {"start": v(324.44, 1882.7) * mm, "end": v(311.44, 1882.7) * mm});
            skLineSegment(sketch, "E26.13.7.1", {"start": v(324.44, 1869.7) * mm, "end": v(324.44, 1882.7) * mm});
            skLineSegment(sketch, "E26.13.7.2", {"start": v(324.44, 1869.7) * mm, "end": v(311.44, 1869.7) * mm});
            skPoint(sketch, "E26.13.7.3", {"position": v(317.94, 1876.2) * mm});
            skLineSegment(sketch, "E26.13.7.4", {"start": v(311.44, 1869.7) * mm, "end": v(311.44, 1882.7) * mm});
            skLineSegment(sketch, "E26.14.0.0", {"start": v(357.44, 132.7) * mm, "end": v(344.44, 132.7) * mm});
            skLineSegment(sketch, "E26.14.0.1", {"start": v(357.44, 119.7) * mm, "end": v(357.44, 132.7) * mm});
            skLineSegment(sketch, "E26.14.0.2", {"start": v(357.44, 119.7) * mm, "end": v(344.44, 119.7) * mm});
            skPoint(sketch, "E26.14.0.3", {"position": v(350.94, 126.2) * mm});
            skLineSegment(sketch, "E26.14.0.4", {"start": v(344.44, 119.7) * mm, "end": v(344.44, 132.7) * mm});
            skLineSegment(sketch, "E26.14.1.0", {"start": v(357.44, 382.7) * mm, "end": v(344.44, 382.7) * mm});
            skLineSegment(sketch, "E26.14.1.1", {"start": v(357.44, 369.7) * mm, "end": v(357.44, 382.7) * mm});
            skLineSegment(sketch, "E26.14.1.2", {"start": v(357.44, 369.7) * mm, "end": v(344.44, 369.7) * mm});
            skPoint(sketch, "E26.14.1.3", {"position": v(350.94, 376.2) * mm});
            skLineSegment(sketch, "E26.14.1.4", {"start": v(344.44, 369.7) * mm, "end": v(344.44, 382.7) * mm});
            skLineSegment(sketch, "E26.14.2.0", {"start": v(357.44, 632.7) * mm, "end": v(344.44, 632.7) * mm});
            skLineSegment(sketch, "E26.14.2.1", {"start": v(357.44, 619.7) * mm, "end": v(357.44, 632.7) * mm});
            skLineSegment(sketch, "E26.14.2.2", {"start": v(357.44, 619.7) * mm, "end": v(344.44, 619.7) * mm});
            skPoint(sketch, "E26.14.2.3", {"position": v(350.94, 626.2) * mm});
            skLineSegment(sketch, "E26.14.2.4", {"start": v(344.44, 619.7) * mm, "end": v(344.44, 632.7) * mm});
            skLineSegment(sketch, "E26.14.3.0", {"start": v(357.44, 882.7) * mm, "end": v(344.44, 882.7) * mm});
            skLineSegment(sketch, "E26.14.3.1", {"start": v(357.44, 869.7) * mm, "end": v(357.44, 882.7) * mm});
            skLineSegment(sketch, "E26.14.3.2", {"start": v(357.44, 869.7) * mm, "end": v(344.44, 869.7) * mm});
            skPoint(sketch, "E26.14.3.3", {"position": v(350.94, 876.2) * mm});
            skLineSegment(sketch, "E26.14.3.4", {"start": v(344.44, 869.7) * mm, "end": v(344.44, 882.7) * mm});
            skLineSegment(sketch, "E26.14.4.0", {"start": v(357.44, 1132.7) * mm, "end": v(344.44, 1132.7) * mm});
            skLineSegment(sketch, "E26.14.4.1", {"start": v(357.44, 1119.7) * mm, "end": v(357.44, 1132.7) * mm});
            skLineSegment(sketch, "E26.14.4.2", {"start": v(357.44, 1119.7) * mm, "end": v(344.44, 1119.7) * mm});
            skPoint(sketch, "E26.14.4.3", {"position": v(350.94, 1126.2) * mm});
            skLineSegment(sketch, "E26.14.4.4", {"start": v(344.44, 1119.7) * mm, "end": v(344.44, 1132.7) * mm});
            skLineSegment(sketch, "E26.14.5.0", {"start": v(357.44, 1382.7) * mm, "end": v(344.44, 1382.7) * mm});
            skLineSegment(sketch, "E26.14.5.1", {"start": v(357.44, 1369.7) * mm, "end": v(357.44, 1382.7) * mm});
            skLineSegment(sketch, "E26.14.5.2", {"start": v(357.44, 1369.7) * mm, "end": v(344.44, 1369.7) * mm});
            skPoint(sketch, "E26.14.5.3", {"position": v(350.94, 1376.2) * mm});
            skLineSegment(sketch, "E26.14.5.4", {"start": v(344.44, 1369.7) * mm, "end": v(344.44, 1382.7) * mm});
            skLineSegment(sketch, "E26.14.6.0", {"start": v(357.44, 1632.7) * mm, "end": v(344.44, 1632.7) * mm});
            skLineSegment(sketch, "E26.14.6.1", {"start": v(357.44, 1619.7) * mm, "end": v(357.44, 1632.7) * mm});
            skLineSegment(sketch, "E26.14.6.2", {"start": v(357.44, 1619.7) * mm, "end": v(344.44, 1619.7) * mm});
            skPoint(sketch, "E26.14.6.3", {"position": v(350.94, 1626.2) * mm});
            skLineSegment(sketch, "E26.14.6.4", {"start": v(344.44, 1619.7) * mm, "end": v(344.44, 1632.7) * mm});
            skLineSegment(sketch, "E26.14.7.0", {"start": v(357.44, 1882.7) * mm, "end": v(344.44, 1882.7) * mm});
            skLineSegment(sketch, "E26.14.7.1", {"start": v(357.44, 1869.7) * mm, "end": v(357.44, 1882.7) * mm});
            skLineSegment(sketch, "E26.14.7.2", {"start": v(357.44, 1869.7) * mm, "end": v(344.44, 1869.7) * mm});
            skPoint(sketch, "E26.14.7.3", {"position": v(350.94, 1876.2) * mm});
            skLineSegment(sketch, "E26.14.7.4", {"start": v(344.44, 1869.7) * mm, "end": v(344.44, 1882.7) * mm});
            skLineSegment(sketch, "E26.direction1", {"start": v(-117.56, 119.7) * mm, "end": v(-84.56, 119.7) * mm, "construction": true});
            skLineSegment(sketch, "E26.direction2", {"start": v(-117.56, 119.7) * mm, "end": v(-117.56, 369.7) * mm, "construction": true});
            skSolve(sketch);
        }
        {
            var Q0;
            Q0 = qSketchRegion(id + "F4", true);
            extrude(context, id + "F5", {"entities" : qUnion([Q0]), "operationType" : NewBodyOperationType.REMOVE, "oppositeDirection" : true, "depth" : 5 * mm, "offsetDistance" : 25 * mm});
        }
    });
